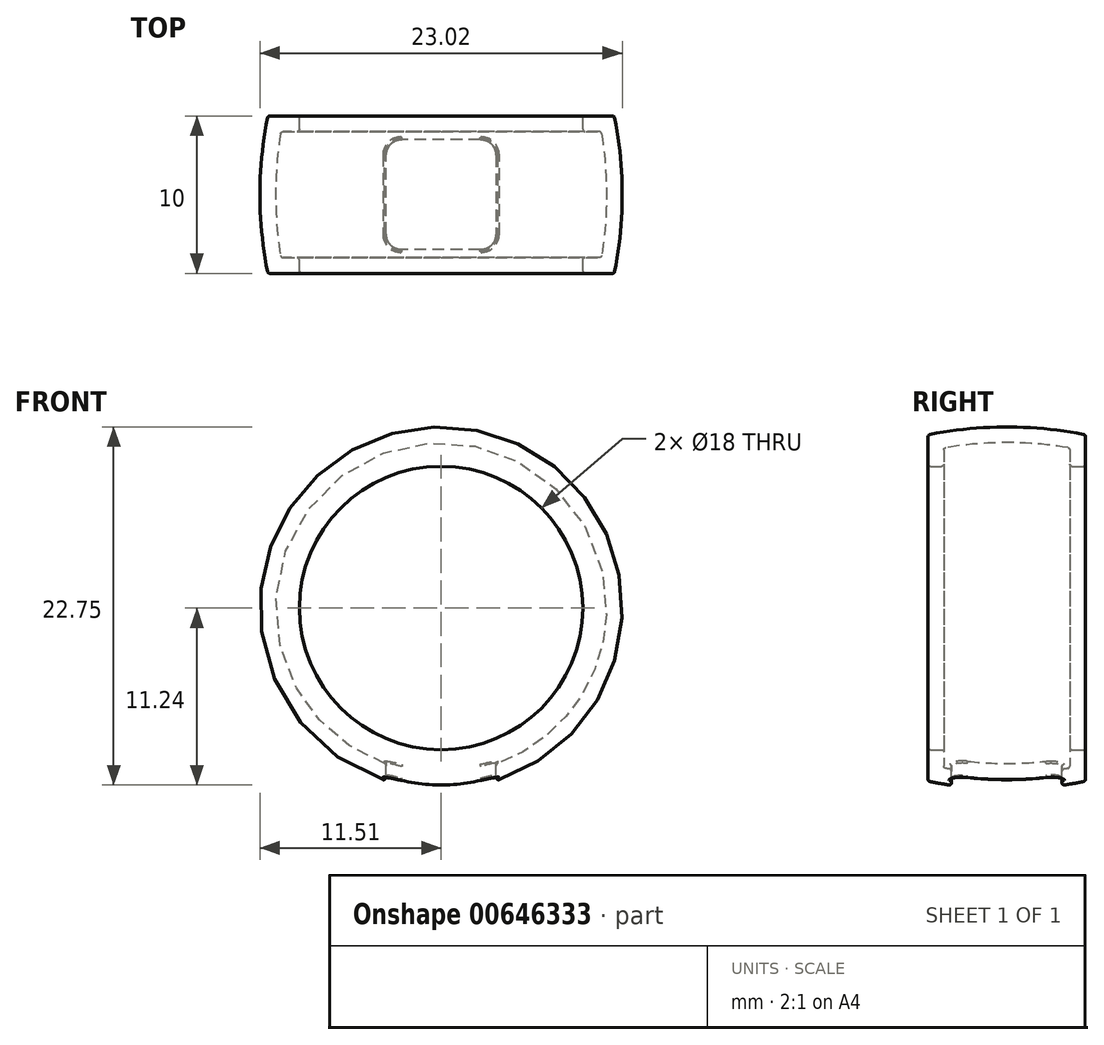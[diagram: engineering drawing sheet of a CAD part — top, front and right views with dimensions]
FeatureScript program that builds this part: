
annotation { "Feature Type Name" : "Feature", "Feature Type Description" : "" }
export const myFeature = defineFeature(function(context is Context, id is Id, definition is map)
    precondition{}
    {
        {
            var Q0;
            Q0=qCreatedBy(makeId("Top.planeOp"),FACE);
            var sketch = newSketch(context, id + "F0", { "sketchPlane" : qUnion([Q0])});
            skLineSegment(sketch, "E0", {"start": v(0, 0) * mm, "end": v(-9, 0) * mm, "construction": true});
            skLineSegment(sketch, "E1", {"start": v(-9, 5) * mm, "end": v(-9, -5) * mm});
            skLineSegment(sketch, "E2", {"start": v(-9, 5) * mm, "end": v(-11, 5) * mm});
            skLineSegment(sketch, "E3", {"start": v(-9, -5) * mm, "end": v(-11, -5) * mm});
            skArc(sketch, "E4", {"start": v(-11, 5) * mm, "mid": v(-11.5, 0) * mm, "end": v(-11, -5) * mm});
            skLineSegment(sketch, "E5", {"start": v(0, 0) * mm, "end": v(0, -20) * mm, "construction": true});
            skSolve(sketch);
        }
        {
            var Q0;
            Q0 = qSketchRegion(id + "F0", true);
            var Q1;
            Q1=sQuery(id+"F0.wireOp",EDGE,"E5");
            revolve(context, id + "F1", {"entities" : qUnion([Q0]), "axis" : qUnion([Q1]), "revolveType" : RevolveType.FULL});
        }
        {
            var Q0;
            Q0=makeQuery(id+"F1.opRevolve","SWEPT_FACE",FACE,{"disambiguationData":[OSD([sQuery(id+"F0.wireOp",EDGE,"E1")])]});
            shell(context, id + "F2", {"entities" : qUnion([Q0]), "thickness" : 1 * mm});
        }
        {
            var Q0;
            Q0=makeQuery(id+"F1.opRevolve","SWEPT_FACE",FACE,{"disambiguationData":[OSD([sQuery(id+"F0.wireOp",EDGE,"E4")])]});
            var Q1;
            Q1=makeQuery(id+"F1.opRevolve","SWEPT_EDGE",EDGE,{"disambiguationData":[OSD([sQuery(id+"F0.wireOp",EDGE,"E3"),sQuery(id+"F0.wireOp",EDGE,"E4")])]});
            var Q2;
            Q2=makeQuery(id+"F1.opRevolve","SWEPT_FACE",FACE,{"disambiguationData":[OSD([sQuery(id+"F0.wireOp",EDGE,"E3")])]});
            var Q3;
            Q3=makeQuery(id+"F1.opRevolve","SWEPT_EDGE",EDGE,{"disambiguationData":[OSD([sQuery(id+"F0.wireOp",EDGE,"E1"),sQuery(id+"F0.wireOp",EDGE,"E3")])]});
            var Q4;
            Q4=makeQuery(id+"F1.opRevolve","SWEPT_FACE",FACE,{"disambiguationData":[OSD([sQuery(id+"F0.wireOp",EDGE,"E2")])]});
            var Q5;
            Q5=makeQuery(id+"F1.opRevolve","SWEPT_EDGE",EDGE,{"disambiguationData":[OSD([sQuery(id+"F0.wireOp",EDGE,"E2"),sQuery(id+"F0.wireOp",EDGE,"E4")])]});
            var Q6;
            Q6=makeQuery(id+"F2.opShell","OFFSET_EDGE",EDGE,{"disambiguationData":[OSD([sQuery(id+"F0.wireOp",EDGE,"E1"),sQuery(id+"F0.wireOp",EDGE,"E2")])]});
            var Q7;
            Q7=makeQuery(id+"F1.opRevolve","SWEPT_EDGE",EDGE,{"disambiguationData":[OSD([sQuery(id+"F0.wireOp",EDGE,"E1"),sQuery(id+"F0.wireOp",EDGE,"E2")])]});
            var Q8;
            Q8=makeQuery(id+"F2.opShell","OFFSET_FACE",FACE,{"disambiguationData":[OSD([sQuery(id+"F0.wireOp",EDGE,"E1")])]});
            var Q9;
            Q9=makeQuery(id+"F2.opShell","OFFSET_EDGE",EDGE,{"disambiguationData":[OSD([sQuery(id+"F0.wireOp",EDGE,"E1"),sQuery(id+"F0.wireOp",EDGE,"E3")])]});
            var Q10;
            Q10=makeQuery(id+"F2.opShell","OFFSET_FACE",FACE,{"disambiguationData":[OSD([sQuery(id+"F0.wireOp",EDGE,"E2")])]});
            var Q11;
            Q11=makeQuery(id+"F2.opShell","OFFSET_EDGE",EDGE,{"disambiguationData":[OSD([sQuery(id+"F0.wireOp",EDGE,"E2"),sQuery(id+"F0.wireOp",EDGE,"E4")])]});
            var Q12;
            Q12=makeQuery(id+"F2.opShell","OFFSET_FACE",FACE,{"disambiguationData":[OSD([sQuery(id+"F0.wireOp",EDGE,"E3")])]});
            var Q13;
            Q13=makeQuery(id+"F2.opShell","OFFSET_FACE",FACE,{"disambiguationData":[OSD([sQuery(id+"F0.wireOp",EDGE,"E4")])]});
            var Q14;
            Q14=makeQuery(id+"F1.opRevolve","SWEPT_FACE",FACE,{"disambiguationData":[OSD([sQuery(id+"F0.wireOp",EDGE,"E1")])]});
            var Q15;
            Q15=makeQuery(id+"F2.opShell","OFFSET_EDGE",EDGE,{"disambiguationData":[OSD([sQuery(id+"F0.wireOp",EDGE,"E3"),sQuery(id+"F0.wireOp",EDGE,"E4")])]});
            fillet(context, id + "F3", {"entities" : qUnion([Q0, Q1, Q2, Q3, Q4, Q5, Q6, Q7, Q8, Q9, Q10, Q11, Q12, Q13, Q14, Q15]), "radius" : 0.15 * mm, "tangentPropagation" : true, "allowEdgeOverflow" : false});
        }
        {
            var Q0;
            Q0=qCreatedBy(makeId("Top.planeOp"),FACE);
            var sketch = newSketch(context, id + "F4", { "sketchPlane" : qUnion([Q0])});
            skLineSegment(sketch, "E6.bottom", {"start": v(2.5, 3.5) * mm, "end": v(-2.5, 3.5) * mm});
            skLineSegment(sketch, "E6.top", {"start": v(2.5, -3.5) * mm, "end": v(-2.5, -3.5) * mm});
            skLineSegment(sketch, "E6.left", {"start": v(3.5, 2.5) * mm, "end": v(3.5, -2.5) * mm});
            skLineSegment(sketch, "E6.right", {"start": v(-3.5, 2.5) * mm, "end": v(-3.5, -2.5) * mm});
            skPoint(sketch, "E6.middle", {"position": v(0, 0) * mm});
            skPoint(sketch, "E7.visualSharp", {"position": v(-3.5, 3.5) * mm});
            skArc(sketch, "E7.filletArc", {"start": v(-2.5, 3.5) * mm, "mid": v(-3.2, 3.2) * mm, "end": v(-3.5, 2.5) * mm});
            skPoint(sketch, "E8.visualSharp", {"position": v(3.5, 3.5) * mm});
            skArc(sketch, "E8.filletArc", {"start": v(3.5, 2.5) * mm, "mid": v(3.2, 3.2) * mm, "end": v(2.5, 3.5) * mm});
            skPoint(sketch, "E9.visualSharp", {"position": v(3.5, -3.5) * mm});
            skArc(sketch, "E9.filletArc", {"start": v(2.5, -3.5) * mm, "mid": v(3.2, -3.2) * mm, "end": v(3.5, -2.5) * mm});
            skPoint(sketch, "E10.visualSharp", {"position": v(-3.5, -3.5) * mm});
            skArc(sketch, "E10.filletArc", {"start": v(-3.5, -2.5) * mm, "mid": v(-3.2, -3.2) * mm, "end": v(-2.5, -3.5) * mm});
            skSolve(sketch);
        }
        {
            var Q0;
            Q0 = qSketchRegion(id + "F4", true);
            extrude(context, id + "F5", {"entities" : qUnion([Q0]), "operationType" : NewBodyOperationType.REMOVE, "endBound" : BoundingType.THROUGH_ALL, "oppositeDirection" : true, "depth" : 25 * mm, "offsetDistance" : 25 * mm});
        }
        {
            var Q0;
            Q0=makeQuery(id+"FbWcAx6KyJmYH2d_1.2.F5.boolean.opBoolean","INTERSECT",EDGE,{"derivedFrom":[makeQuery(id+"F1.opRevolve","SWEPT_FACE",FACE,{"disambiguationData":[OSD([sQuery(id+"F0.wireOp",EDGE,"E4")])]}),makeQuery(id+"FbWcAx6KyJmYH2d_1.2.F5.opExtrude","SWEPT_FACE",FACE,{"disambiguationData":[OSD([sQuery(id+"F4.wireOp",EDGE,"E6.right")])]})]});
            var Q1;
            {var subQ0=sQuery(id+"F0.wireOp",EDGE,"E3");Q1=makeQuery(id+"F3.opFillet","BLEND_EDGE",EDGE,{"blendedFrom":[makeQuery(id+"F1.opRevolve","SWEPT_EDGE",EDGE,{"disambiguationData":[OSD([sQuery(id+"F0.wireOp",EDGE,"E1"),subQ0])]}),makeQuery(id+"F1.opRevolve","SWEPT_FACE",FACE,{"disambiguationData":[OSD([subQ0])]})],"blendedInto":[makeQuery(id+"F1.opRevolve","SWEPT_FACE",FACE,{"disambiguationData":[OSD([subQ0])]})]});}
            var Q2;
            {var subQ0=sQuery(id+"F0.wireOp",EDGE,"E4");var subQ1=sQuery(id+"F0.wireOp",EDGE,"E3");Q2=makeQuery(id+"F3.opFillet","BLEND_FACE",FACE,{"disambiguationData":[OSD([subQ1,subQ0]),TDD([makeQuery(id+"F1.opRevolve","SWEPT_EDGE",EDGE,{"disambiguationData":[OSD([subQ1,subQ0])]})])]});}
            var Q3;
            {var subQ0=sQuery(id+"F0.wireOp",EDGE,"E1");Q3=makeQuery(id+"F3.opFillet","BLEND_EDGE",EDGE,{"blendedFrom":[makeQuery(id+"F1.opRevolve","SWEPT_EDGE",EDGE,{"disambiguationData":[OSD([subQ0,sQuery(id+"F0.wireOp",EDGE,"E3")])]}),makeQuery(id+"F1.opRevolve","SWEPT_FACE",FACE,{"disambiguationData":[OSD([subQ0])]})],"blendedInto":[makeQuery(id+"F1.opRevolve","SWEPT_FACE",FACE,{"disambiguationData":[OSD([subQ0])]})]});}
            var Q4;
            {var subQ0=sQuery(id+"F0.wireOp",EDGE,"E1");Q4=makeQuery(id+"F3.opFillet","BLEND_EDGE",EDGE,{"blendedFrom":[makeQuery(id+"F2.opShell","OFFSET_EDGE",EDGE,{"disambiguationData":[OSD([subQ0,sQuery(id+"F0.wireOp",EDGE,"E2")])]}),makeQuery(id+"F2.opShell","OFFSET_FACE",FACE,{"disambiguationData":[OSD([subQ0])]})],"blendedInto":[makeQuery(id+"F2.opShell","OFFSET_FACE",FACE,{"disambiguationData":[OSD([subQ0])]})]});}
            var Q5;
            {var subQ0=sQuery(id+"F0.wireOp",EDGE,"E4");var subQ1=sQuery(id+"F0.wireOp",EDGE,"E2");Q5=makeQuery(id+"F3.opFillet","BLEND_FACE",FACE,{"disambiguationData":[OSD([subQ1,subQ0]),TDD([makeQuery(id+"F1.opRevolve","SWEPT_EDGE",EDGE,{"disambiguationData":[OSD([subQ1,subQ0])]})])]});}
            var Q6;
            {var subQ0=sQuery(id+"F0.wireOp",EDGE,"E3");var subQ1=sQuery(id+"F0.wireOp",EDGE,"E1");Q6=makeQuery(id+"F3.opFillet","BLEND_FACE",FACE,{"disambiguationData":[OSD([subQ1,subQ0]),TDD([makeQuery(id+"F2.opShell","OFFSET_EDGE",EDGE,{"disambiguationData":[OSD([subQ1,subQ0])]})])]});}
            var Q7;
            {var subQ0=sQuery(id+"F0.wireOp",EDGE,"E4");var subQ1=sQuery(id+"F0.wireOp",EDGE,"E2");Q7=makeQuery(id+"F3.opFillet","BLEND_FACE",FACE,{"disambiguationData":[OSD([subQ1,subQ0]),TDD([makeQuery(id+"F2.opShell","OFFSET_EDGE",EDGE,{"disambiguationData":[OSD([subQ1,subQ0])]})])]});}
            var Q8;
            {var subQ0=sQuery(id+"F0.wireOp",EDGE,"E4");Q8=makeQuery(id+"F3.opFillet","BLEND_EDGE",EDGE,{"blendedFrom":[makeQuery(id+"F1.opRevolve","SWEPT_EDGE",EDGE,{"disambiguationData":[OSD([sQuery(id+"F0.wireOp",EDGE,"E2"),subQ0])]}),makeQuery(id+"F1.opRevolve","SWEPT_FACE",FACE,{"disambiguationData":[OSD([subQ0])]})],"blendedInto":[makeQuery(id+"F1.opRevolve","SWEPT_FACE",FACE,{"disambiguationData":[OSD([subQ0])]})]});}
            var Q9;
            Q9=makeQuery(id+"FbWcAx6KyJmYH2d_1.1.F5.boolean.opBoolean","INTERSECT",EDGE,{"derivedFrom":[makeQuery(id+"F1.opRevolve","SWEPT_FACE",FACE,{"disambiguationData":[OSD([sQuery(id+"F0.wireOp",EDGE,"E4")])]}),makeQuery(id+"FbWcAx6KyJmYH2d_1.1.F5.opExtrude","SWEPT_FACE",FACE,{"disambiguationData":[OSD([sQuery(id+"F4.wireOp",EDGE,"E6.bottom")])]})]});
            var Q10;
            Q10=makeQuery(id+"FbWcAx6KyJmYH2d_1.1.F5.boolean.opBoolean","COPY",FACE,{"derivedFrom":makeQuery(id+"FbWcAx6KyJmYH2d_1.1.F5.opExtrude","SWEPT_FACE",FACE,{"disambiguationData":[OSD([sQuery(id+"F4.wireOp",EDGE,"E9.filletArc")])]})});
            var Q11;
            Q11=makeQuery(id+"FbWcAx6KyJmYH2d_1.1.F5.boolean.opBoolean","INTERSECT",EDGE,{"derivedFrom":[makeQuery(id+"F1.opRevolve","SWEPT_FACE",FACE,{"disambiguationData":[OSD([sQuery(id+"F0.wireOp",EDGE,"E4")])]}),makeQuery(id+"FbWcAx6KyJmYH2d_1.1.F5.opExtrude","SWEPT_FACE",FACE,{"disambiguationData":[OSD([sQuery(id+"F4.wireOp",EDGE,"E6.top")])]})]});
            var Q12;
            Q12=makeQuery(id+"FbWcAx6KyJmYH2d_1.3.F5.boolean.opBoolean","INTERSECT",EDGE,{"derivedFrom":[makeQuery(id+"F1.opRevolve","SWEPT_FACE",FACE,{"disambiguationData":[OSD([sQuery(id+"F0.wireOp",EDGE,"E4")])]}),makeQuery(id+"FbWcAx6KyJmYH2d_1.3.F5.opExtrude","SWEPT_FACE",FACE,{"disambiguationData":[OSD([sQuery(id+"F4.wireOp",EDGE,"E6.top")])]})]});
            var Q13;
            Q13=makeQuery(id+"FbWcAx6KyJmYH2d_1.2.F5.boolean.opBoolean","COPY",FACE,{"derivedFrom":makeQuery(id+"FbWcAx6KyJmYH2d_1.2.F5.opExtrude","SWEPT_FACE",FACE,{"disambiguationData":[OSD([sQuery(id+"F4.wireOp",EDGE,"E6.right")])]})});
            var Q14;
            Q14=makeQuery(id+"FbWcAx6KyJmYH2d_1.3.F5.boolean.opBoolean","COPY",FACE,{"derivedFrom":makeQuery(id+"FbWcAx6KyJmYH2d_1.3.F5.opExtrude","SWEPT_FACE",FACE,{"disambiguationData":[OSD([sQuery(id+"F4.wireOp",EDGE,"E10.filletArc")])]})});
            var Q15;
            Q15=makeQuery(id+"FbWcAx6KyJmYH2d_1.2.F5.boolean.opBoolean","COPY",FACE,{"derivedFrom":makeQuery(id+"FbWcAx6KyJmYH2d_1.2.F5.opExtrude","SWEPT_FACE",FACE,{"disambiguationData":[OSD([sQuery(id+"F4.wireOp",EDGE,"E6.bottom")])]})});
            var Q16;
            Q16=makeQuery(id+"FbWcAx6KyJmYH2d_1.2.F5.boolean.opBoolean","COPY",FACE,{"derivedFrom":makeQuery(id+"FbWcAx6KyJmYH2d_1.2.F5.opExtrude","SWEPT_FACE",FACE,{"disambiguationData":[OSD([sQuery(id+"F4.wireOp",EDGE,"E8.filletArc")])]})});
            var Q17;
            Q17=makeQuery(id+"FbWcAx6KyJmYH2d_1.2.F5.boolean.opBoolean","COPY",FACE,{"derivedFrom":makeQuery(id+"FbWcAx6KyJmYH2d_1.2.F5.opExtrude","SWEPT_FACE",FACE,{"disambiguationData":[OSD([sQuery(id+"F4.wireOp",EDGE,"E9.filletArc")])]})});
            var Q18;
            Q18=makeQuery(id+"FbWcAx6KyJmYH2d_1.2.F5.boolean.opBoolean","INTERSECT",EDGE,{"derivedFrom":[makeQuery(id+"F1.opRevolve","SWEPT_FACE",FACE,{"disambiguationData":[OSD([sQuery(id+"F0.wireOp",EDGE,"E4")])]}),makeQuery(id+"FbWcAx6KyJmYH2d_1.2.F5.opExtrude","SWEPT_FACE",FACE,{"disambiguationData":[OSD([sQuery(id+"F4.wireOp",EDGE,"E6.bottom")])]})]});
            var Q19;
            Q19=makeQuery(id+"FbWcAx6KyJmYH2d_1.4.F5.boolean.opBoolean","INTERSECT",EDGE,{"derivedFrom":[makeQuery(id+"F1.opRevolve","SWEPT_FACE",FACE,{"disambiguationData":[OSD([sQuery(id+"F0.wireOp",EDGE,"E4")])]}),makeQuery(id+"FbWcAx6KyJmYH2d_1.4.F5.opExtrude","SWEPT_FACE",FACE,{"disambiguationData":[OSD([sQuery(id+"F4.wireOp",EDGE,"E6.right")])]})]});
            var Q20;
            {var subQ0=sQuery(id+"F0.wireOp",EDGE,"E2");Q20=makeQuery(id+"F3.opFillet","BLEND_EDGE",EDGE,{"blendedFrom":[makeQuery(id+"F2.opShell","OFFSET_EDGE",EDGE,{"disambiguationData":[OSD([sQuery(id+"F0.wireOp",EDGE,"E1"),subQ0])]}),makeQuery(id+"F2.opShell","OFFSET_FACE",FACE,{"disambiguationData":[OSD([subQ0])]})],"blendedInto":[makeQuery(id+"F2.opShell","OFFSET_FACE",FACE,{"disambiguationData":[OSD([subQ0])]})]});}
            var Q21;
            {var subQ0=sQuery(id+"F0.wireOp",EDGE,"E4");Q21=makeQuery(id+"F3.opFillet","BLEND_EDGE",EDGE,{"blendedFrom":[makeQuery(id+"F2.opShell","OFFSET_EDGE",EDGE,{"disambiguationData":[OSD([sQuery(id+"F0.wireOp",EDGE,"E2"),subQ0])]}),makeQuery(id+"F2.opShell","OFFSET_FACE",FACE,{"disambiguationData":[OSD([subQ0])]})],"blendedInto":[makeQuery(id+"F2.opShell","OFFSET_FACE",FACE,{"disambiguationData":[OSD([subQ0])]})]});}
            var Q22;
            Q22=makeQuery(id+"F1.opRevolve","SWEPT_FACE",FACE,{"disambiguationData":[OSD([sQuery(id+"F0.wireOp",EDGE,"E3")])]});
            var Q23;
            {var subQ0=sQuery(id+"F0.wireOp",EDGE,"E3");var subQ1=sQuery(id+"F0.wireOp",EDGE,"E1");Q23=makeQuery(id+"F3.opFillet","BLEND_FACE",FACE,{"disambiguationData":[OSD([subQ1,subQ0]),TDD([makeQuery(id+"F1.opRevolve","SWEPT_EDGE",EDGE,{"disambiguationData":[OSD([subQ1,subQ0])]})])]});}
            var Q24;
            {var subQ0=sQuery(id+"F0.wireOp",EDGE,"E3");Q24=makeQuery(id+"F3.opFillet","BLEND_EDGE",EDGE,{"blendedFrom":[makeQuery(id+"F1.opRevolve","SWEPT_EDGE",EDGE,{"disambiguationData":[OSD([subQ0,sQuery(id+"F0.wireOp",EDGE,"E4")])]}),makeQuery(id+"F1.opRevolve","SWEPT_FACE",FACE,{"disambiguationData":[OSD([subQ0])]})],"blendedInto":[makeQuery(id+"F1.opRevolve","SWEPT_FACE",FACE,{"disambiguationData":[OSD([subQ0])]})]});}
            var Q25;
            {var subQ0=sQuery(id+"F0.wireOp",EDGE,"E2");var subQ1=sQuery(id+"F0.wireOp",EDGE,"E1");Q25=makeQuery(id+"F3.opFillet","BLEND_FACE",FACE,{"disambiguationData":[OSD([subQ1,subQ0]),TDD([makeQuery(id+"F2.opShell","OFFSET_EDGE",EDGE,{"disambiguationData":[OSD([subQ1,subQ0])]})])]});}
            var Q26;
            {var subQ0=sQuery(id+"F0.wireOp",EDGE,"E2");var subQ1=sQuery(id+"F0.wireOp",EDGE,"E1");Q26=makeQuery(id+"F3.opFillet","BLEND_FACE",FACE,{"disambiguationData":[OSD([subQ1,subQ0]),TDD([makeQuery(id+"F1.opRevolve","SWEPT_EDGE",EDGE,{"disambiguationData":[OSD([subQ1,subQ0])]})])]});}
            var Q27;
            {var subQ0=sQuery(id+"F0.wireOp",EDGE,"E1");Q27=makeQuery(id+"F3.opFillet","BLEND_EDGE",EDGE,{"blendedFrom":[makeQuery(id+"F2.opShell","OFFSET_EDGE",EDGE,{"disambiguationData":[OSD([subQ0,sQuery(id+"F0.wireOp",EDGE,"E3")])]}),makeQuery(id+"F1.opRevolve","SWEPT_FACE",FACE,{"disambiguationData":[OSD([subQ0])]})],"blendedInto":[makeQuery(id+"F1.opRevolve","SWEPT_FACE",FACE,{"disambiguationData":[OSD([subQ0])]})]});}
            var Q28;
            {var subQ0=sQuery(id+"F0.wireOp",EDGE,"E1");Q28=makeQuery(id+"F3.opFillet","BLEND_EDGE",EDGE,{"blendedFrom":[makeQuery(id+"F1.opRevolve","SWEPT_EDGE",EDGE,{"disambiguationData":[OSD([subQ0,sQuery(id+"F0.wireOp",EDGE,"E2")])]}),makeQuery(id+"F2.opShell","OFFSET_FACE",FACE,{"disambiguationData":[OSD([subQ0])]})],"blendedInto":[makeQuery(id+"F2.opShell","OFFSET_FACE",FACE,{"disambiguationData":[OSD([subQ0])]})]});}
            var Q29;
            Q29=makeQuery(id+"FbWcAx6KyJmYH2d_1.6.F5.boolean.opBoolean","INTERSECT",EDGE,{"derivedFrom":[makeQuery(id+"F2.opShell","OFFSET_FACE",FACE,{"disambiguationData":[OSD([sQuery(id+"F0.wireOp",EDGE,"E4")])]}),makeQuery(id+"FbWcAx6KyJmYH2d_1.6.F5.opExtrude","SWEPT_FACE",FACE,{"disambiguationData":[OSD([sQuery(id+"F4.wireOp",EDGE,"E6.left")])]})]});
            var Q30;
            Q30=makeQuery(id+"FbWcAx6KyJmYH2d_1.1.F5.boolean.opBoolean","COPY",FACE,{"derivedFrom":makeQuery(id+"FbWcAx6KyJmYH2d_1.1.F5.opExtrude","SWEPT_FACE",FACE,{"disambiguationData":[OSD([sQuery(id+"F4.wireOp",EDGE,"E6.right")])]})});
            var Q31;
            {var subQ0=sQuery(id+"F0.wireOp",EDGE,"E4");Q31=makeQuery(id+"F3.opFillet","BLEND_EDGE",EDGE,{"blendedFrom":[makeQuery(id+"F1.opRevolve","SWEPT_EDGE",EDGE,{"disambiguationData":[OSD([sQuery(id+"F0.wireOp",EDGE,"E3"),subQ0])]}),makeQuery(id+"F1.opRevolve","SWEPT_FACE",FACE,{"disambiguationData":[OSD([subQ0])]})],"blendedInto":[makeQuery(id+"F1.opRevolve","SWEPT_FACE",FACE,{"disambiguationData":[OSD([subQ0])]})]});}
            var Q32;
            Q32=makeQuery(id+"F1.opRevolve","SWEPT_FACE",FACE,{"disambiguationData":[OSD([sQuery(id+"F0.wireOp",EDGE,"E1")])]});
            var Q33;
            Q33=makeQuery(id+"FbWcAx6KyJmYH2d_1.2.F5.boolean.opBoolean","INTERSECT",EDGE,{"derivedFrom":[makeQuery(id+"F2.opShell","OFFSET_FACE",FACE,{"disambiguationData":[OSD([sQuery(id+"F0.wireOp",EDGE,"E4")])]}),makeQuery(id+"FbWcAx6KyJmYH2d_1.2.F5.opExtrude","SWEPT_FACE",FACE,{"disambiguationData":[OSD([sQuery(id+"F4.wireOp",EDGE,"E6.right")])]})]});
            var Q34;
            Q34=makeQuery(id+"FbWcAx6KyJmYH2d_1.1.F5.boolean.opBoolean","INTERSECT",EDGE,{"derivedFrom":[makeQuery(id+"F1.opRevolve","SWEPT_FACE",FACE,{"disambiguationData":[OSD([sQuery(id+"F0.wireOp",EDGE,"E4")])]}),makeQuery(id+"FbWcAx6KyJmYH2d_1.1.F5.opExtrude","SWEPT_FACE",FACE,{"disambiguationData":[OSD([sQuery(id+"F4.wireOp",EDGE,"E6.left")])]})]});
            var Q35;
            Q35=makeQuery(id+"FbWcAx6KyJmYH2d_1.2.F5.boolean.opBoolean","INTERSECT",EDGE,{"derivedFrom":[makeQuery(id+"F1.opRevolve","SWEPT_FACE",FACE,{"disambiguationData":[OSD([sQuery(id+"F0.wireOp",EDGE,"E4")])]}),makeQuery(id+"FbWcAx6KyJmYH2d_1.2.F5.opExtrude","SWEPT_FACE",FACE,{"disambiguationData":[OSD([sQuery(id+"F4.wireOp",EDGE,"E6.top")])]})]});
            var Q36;
            Q36=makeQuery(id+"FbWcAx6KyJmYH2d_1.2.F5.boolean.opBoolean","INTERSECT",EDGE,{"derivedFrom":[makeQuery(id+"F1.opRevolve","SWEPT_FACE",FACE,{"disambiguationData":[OSD([sQuery(id+"F0.wireOp",EDGE,"E4")])]}),makeQuery(id+"FbWcAx6KyJmYH2d_1.2.F5.opExtrude","SWEPT_FACE",FACE,{"disambiguationData":[OSD([sQuery(id+"F4.wireOp",EDGE,"E6.left")])]})]});
            var Q37;
            Q37=makeQuery(id+"FbWcAx6KyJmYH2d_1.3.F5.boolean.opBoolean","INTERSECT",EDGE,{"derivedFrom":[makeQuery(id+"F2.opShell","OFFSET_FACE",FACE,{"disambiguationData":[OSD([sQuery(id+"F0.wireOp",EDGE,"E4")])]}),makeQuery(id+"FbWcAx6KyJmYH2d_1.3.F5.opExtrude","SWEPT_FACE",FACE,{"disambiguationData":[OSD([sQuery(id+"F4.wireOp",EDGE,"E6.left")])]})]});
            var Q38;
            Q38=makeQuery(id+"FbWcAx6KyJmYH2d_1.3.F5.boolean.opBoolean","INTERSECT",EDGE,{"derivedFrom":[makeQuery(id+"F1.opRevolve","SWEPT_FACE",FACE,{"disambiguationData":[OSD([sQuery(id+"F0.wireOp",EDGE,"E4")])]}),makeQuery(id+"FbWcAx6KyJmYH2d_1.3.F5.opExtrude","SWEPT_FACE",FACE,{"disambiguationData":[OSD([sQuery(id+"F4.wireOp",EDGE,"E6.right")])]})]});
            var Q39;
            Q39=makeQuery(id+"FbWcAx6KyJmYH2d_1.3.F5.boolean.opBoolean","COPY",FACE,{"derivedFrom":makeQuery(id+"FbWcAx6KyJmYH2d_1.3.F5.opExtrude","SWEPT_FACE",FACE,{"disambiguationData":[OSD([sQuery(id+"F4.wireOp",EDGE,"E6.bottom")])]})});
            var Q40;
            Q40=makeQuery(id+"FbWcAx6KyJmYH2d_1.3.F5.boolean.opBoolean","COPY",FACE,{"derivedFrom":makeQuery(id+"FbWcAx6KyJmYH2d_1.3.F5.opExtrude","SWEPT_FACE",FACE,{"disambiguationData":[OSD([sQuery(id+"F4.wireOp",EDGE,"E6.top")])]})});
            var Q41;
            Q41=makeQuery(id+"FbWcAx6KyJmYH2d_1.3.F5.boolean.opBoolean","COPY",FACE,{"derivedFrom":makeQuery(id+"FbWcAx6KyJmYH2d_1.3.F5.opExtrude","SWEPT_FACE",FACE,{"disambiguationData":[OSD([sQuery(id+"F4.wireOp",EDGE,"E6.left")])]})});
            var Q42;
            Q42=makeQuery(id+"FbWcAx6KyJmYH2d_1.2.F5.boolean.opBoolean","INTERSECT",EDGE,{"derivedFrom":[makeQuery(id+"F2.opShell","OFFSET_FACE",FACE,{"disambiguationData":[OSD([sQuery(id+"F0.wireOp",EDGE,"E4")])]}),makeQuery(id+"FbWcAx6KyJmYH2d_1.2.F5.opExtrude","SWEPT_FACE",FACE,{"disambiguationData":[OSD([sQuery(id+"F4.wireOp",EDGE,"E6.bottom")])]})]});
            var Q43;
            Q43=makeQuery(id+"FbWcAx6KyJmYH2d_1.4.F5.boolean.opBoolean","INTERSECT",EDGE,{"derivedFrom":[makeQuery(id+"F2.opShell","OFFSET_FACE",FACE,{"disambiguationData":[OSD([sQuery(id+"F0.wireOp",EDGE,"E4")])]}),makeQuery(id+"FbWcAx6KyJmYH2d_1.4.F5.opExtrude","SWEPT_FACE",FACE,{"disambiguationData":[OSD([sQuery(id+"F4.wireOp",EDGE,"E6.left")])]})]});
            var Q44;
            Q44=makeQuery(id+"FbWcAx6KyJmYH2d_1.1.F5.boolean.opBoolean","COPY",FACE,{"derivedFrom":makeQuery(id+"FbWcAx6KyJmYH2d_1.1.F5.opExtrude","SWEPT_FACE",FACE,{"disambiguationData":[OSD([sQuery(id+"F4.wireOp",EDGE,"E7.filletArc")])]})});
            var Q45;
            Q45=makeQuery(id+"FbWcAx6KyJmYH2d_1.1.F5.boolean.opBoolean","COPY",FACE,{"derivedFrom":makeQuery(id+"FbWcAx6KyJmYH2d_1.1.F5.opExtrude","SWEPT_FACE",FACE,{"disambiguationData":[OSD([sQuery(id+"F4.wireOp",EDGE,"E6.left")])]})});
            var Q46;
            Q46=makeQuery(id+"FbWcAx6KyJmYH2d_1.1.F5.boolean.opBoolean","COPY",FACE,{"derivedFrom":makeQuery(id+"FbWcAx6KyJmYH2d_1.1.F5.opExtrude","SWEPT_FACE",FACE,{"disambiguationData":[OSD([sQuery(id+"F4.wireOp",EDGE,"E6.bottom")])]})});
            var Q47;
            Q47=makeQuery(id+"FbWcAx6KyJmYH2d_1.1.F5.boolean.opBoolean","INTERSECT",EDGE,{"derivedFrom":[makeQuery(id+"F1.opRevolve","SWEPT_FACE",FACE,{"disambiguationData":[OSD([sQuery(id+"F0.wireOp",EDGE,"E4")])]}),makeQuery(id+"FbWcAx6KyJmYH2d_1.1.F5.opExtrude","SWEPT_FACE",FACE,{"disambiguationData":[OSD([sQuery(id+"F4.wireOp",EDGE,"E6.right")])]})]});
            var Q48;
            Q48=makeQuery(id+"F5.boolean.opBoolean","INTERSECT",EDGE,{"derivedFrom":[makeQuery(id+"F2.opShell","OFFSET_FACE",FACE,{"disambiguationData":[OSD([sQuery(id+"F0.wireOp",EDGE,"E4")])]}),makeQuery(id+"F5.opExtrude","SWEPT_FACE",FACE,{"disambiguationData":[OSD([sQuery(id+"F4.wireOp",EDGE,"E6.bottom")])]})]});
            var Q49;
            Q49=makeQuery(id+"F5.boolean.opBoolean","INTERSECT",EDGE,{"derivedFrom":[makeQuery(id+"F1.opRevolve","SWEPT_FACE",FACE,{"disambiguationData":[OSD([sQuery(id+"F0.wireOp",EDGE,"E4")])]}),makeQuery(id+"F5.opExtrude","SWEPT_FACE",FACE,{"disambiguationData":[OSD([sQuery(id+"F4.wireOp",EDGE,"E6.bottom")])]})]});
            var Q50;
            Q50=makeQuery(id+"F5.boolean.opBoolean","COPY",FACE,{"derivedFrom":makeQuery(id+"F5.opExtrude","SWEPT_FACE",FACE,{"disambiguationData":[OSD([sQuery(id+"F4.wireOp",EDGE,"E10.filletArc")])]})});
            var Q51;
            Q51=makeQuery(id+"F5.boolean.opBoolean","COPY",FACE,{"derivedFrom":makeQuery(id+"F5.opExtrude","SWEPT_FACE",FACE,{"disambiguationData":[OSD([sQuery(id+"F4.wireOp",EDGE,"E7.filletArc")])]})});
            var Q52;
            Q52=makeQuery(id+"F5.boolean.opBoolean","COPY",FACE,{"derivedFrom":makeQuery(id+"F5.opExtrude","SWEPT_FACE",FACE,{"disambiguationData":[OSD([sQuery(id+"F4.wireOp",EDGE,"E6.right")])]})});
            var Q53;
            Q53=makeQuery(id+"F5.boolean.opBoolean","COPY",FACE,{"derivedFrom":makeQuery(id+"F5.opExtrude","SWEPT_FACE",FACE,{"disambiguationData":[OSD([sQuery(id+"F4.wireOp",EDGE,"E6.bottom")])]})});
            var Q54;
            Q54=makeQuery(id+"F5.boolean.opBoolean","INTERSECT",EDGE,{"derivedFrom":[makeQuery(id+"F2.opShell","OFFSET_FACE",FACE,{"disambiguationData":[OSD([sQuery(id+"F0.wireOp",EDGE,"E4")])]}),makeQuery(id+"F5.opExtrude","SWEPT_FACE",FACE,{"disambiguationData":[OSD([sQuery(id+"F4.wireOp",EDGE,"E6.right")])]})]});
            var Q55;
            Q55=makeQuery(id+"F5.boolean.opBoolean","INTERSECT",EDGE,{"derivedFrom":[makeQuery(id+"F1.opRevolve","SWEPT_FACE",FACE,{"disambiguationData":[OSD([sQuery(id+"F0.wireOp",EDGE,"E4")])]}),makeQuery(id+"F5.opExtrude","SWEPT_FACE",FACE,{"disambiguationData":[OSD([sQuery(id+"F4.wireOp",EDGE,"E6.right")])]})]});
            var Q56;
            Q56=makeQuery(id+"F2.opShell","OFFSET_FACE",FACE,{"disambiguationData":[OSD([sQuery(id+"F0.wireOp",EDGE,"E1")])]});
            var Q57;
            {var subQ0=sQuery(id+"F0.wireOp",EDGE,"E2");Q57=makeQuery(id+"F3.opFillet","BLEND_EDGE",EDGE,{"blendedFrom":[makeQuery(id+"F2.opShell","OFFSET_EDGE",EDGE,{"disambiguationData":[OSD([subQ0,sQuery(id+"F0.wireOp",EDGE,"E4")])]}),makeQuery(id+"F2.opShell","OFFSET_FACE",FACE,{"disambiguationData":[OSD([subQ0])]})],"blendedInto":[makeQuery(id+"F2.opShell","OFFSET_FACE",FACE,{"disambiguationData":[OSD([subQ0])]})]});}
            var Q58;
            Q58=makeQuery(id+"FbWcAx6KyJmYH2d_1.6.F5.boolean.opBoolean","INTERSECT",EDGE,{"derivedFrom":[makeQuery(id+"F2.opShell","OFFSET_FACE",FACE,{"disambiguationData":[OSD([sQuery(id+"F0.wireOp",EDGE,"E4")])]}),makeQuery(id+"FbWcAx6KyJmYH2d_1.6.F5.opExtrude","SWEPT_FACE",FACE,{"disambiguationData":[OSD([sQuery(id+"F4.wireOp",EDGE,"E9.filletArc")])]})]});
            var Q59;
            Q59=makeQuery(id+"FbWcAx6KyJmYH2d_1.6.F5.boolean.opBoolean","INTERSECT",EDGE,{"derivedFrom":[makeQuery(id+"F1.opRevolve","SWEPT_FACE",FACE,{"disambiguationData":[OSD([sQuery(id+"F0.wireOp",EDGE,"E4")])]}),makeQuery(id+"FbWcAx6KyJmYH2d_1.6.F5.opExtrude","SWEPT_FACE",FACE,{"disambiguationData":[OSD([sQuery(id+"F4.wireOp",EDGE,"E8.filletArc")])]})]});
            var Q60;
            Q60=makeQuery(id+"FbWcAx6KyJmYH2d_1.6.F5.boolean.opBoolean","INTERSECT",EDGE,{"derivedFrom":[makeQuery(id+"F2.opShell","OFFSET_FACE",FACE,{"disambiguationData":[OSD([sQuery(id+"F0.wireOp",EDGE,"E4")])]}),makeQuery(id+"FbWcAx6KyJmYH2d_1.6.F5.opExtrude","SWEPT_FACE",FACE,{"disambiguationData":[OSD([sQuery(id+"F4.wireOp",EDGE,"E8.filletArc")])]})]});
            var Q61;
            Q61=makeQuery(id+"FbWcAx6KyJmYH2d_1.6.F5.boolean.opBoolean","INTERSECT",EDGE,{"derivedFrom":[makeQuery(id+"F2.opShell","OFFSET_FACE",FACE,{"disambiguationData":[OSD([sQuery(id+"F0.wireOp",EDGE,"E4")])]}),makeQuery(id+"FbWcAx6KyJmYH2d_1.6.F5.opExtrude","SWEPT_FACE",FACE,{"disambiguationData":[OSD([sQuery(id+"F4.wireOp",EDGE,"E7.filletArc")])]})]});
            var Q62;
            Q62=makeQuery(id+"FbWcAx6KyJmYH2d_1.6.F5.boolean.opBoolean","INTERSECT",EDGE,{"derivedFrom":[makeQuery(id+"F1.opRevolve","SWEPT_FACE",FACE,{"disambiguationData":[OSD([sQuery(id+"F0.wireOp",EDGE,"E4")])]}),makeQuery(id+"FbWcAx6KyJmYH2d_1.6.F5.opExtrude","SWEPT_FACE",FACE,{"disambiguationData":[OSD([sQuery(id+"F4.wireOp",EDGE,"E7.filletArc")])]})]});
            var Q63;
            Q63=makeQuery(id+"FbWcAx6KyJmYH2d_1.5.F5.boolean.opBoolean","INTERSECT",EDGE,{"derivedFrom":[makeQuery(id+"F2.opShell","OFFSET_FACE",FACE,{"disambiguationData":[OSD([sQuery(id+"F0.wireOp",EDGE,"E4")])]}),makeQuery(id+"FbWcAx6KyJmYH2d_1.5.F5.opExtrude","SWEPT_FACE",FACE,{"disambiguationData":[OSD([sQuery(id+"F4.wireOp",EDGE,"E9.filletArc")])]})]});
            var Q64;
            Q64=makeQuery(id+"FbWcAx6KyJmYH2d_1.5.F5.boolean.opBoolean","INTERSECT",EDGE,{"derivedFrom":[makeQuery(id+"F1.opRevolve","SWEPT_FACE",FACE,{"disambiguationData":[OSD([sQuery(id+"F0.wireOp",EDGE,"E4")])]}),makeQuery(id+"FbWcAx6KyJmYH2d_1.5.F5.opExtrude","SWEPT_FACE",FACE,{"disambiguationData":[OSD([sQuery(id+"F4.wireOp",EDGE,"E8.filletArc")])]})]});
            var Q65;
            Q65=makeQuery(id+"FbWcAx6KyJmYH2d_1.5.F5.boolean.opBoolean","INTERSECT",EDGE,{"derivedFrom":[makeQuery(id+"F2.opShell","OFFSET_FACE",FACE,{"disambiguationData":[OSD([sQuery(id+"F0.wireOp",EDGE,"E4")])]}),makeQuery(id+"FbWcAx6KyJmYH2d_1.5.F5.opExtrude","SWEPT_FACE",FACE,{"disambiguationData":[OSD([sQuery(id+"F4.wireOp",EDGE,"E8.filletArc")])]})]});
            var Q66;
            Q66=makeQuery(id+"FbWcAx6KyJmYH2d_1.5.F5.boolean.opBoolean","INTERSECT",EDGE,{"derivedFrom":[makeQuery(id+"F2.opShell","OFFSET_FACE",FACE,{"disambiguationData":[OSD([sQuery(id+"F0.wireOp",EDGE,"E4")])]}),makeQuery(id+"FbWcAx6KyJmYH2d_1.5.F5.opExtrude","SWEPT_FACE",FACE,{"disambiguationData":[OSD([sQuery(id+"F4.wireOp",EDGE,"E7.filletArc")])]})]});
            var Q67;
            Q67=makeQuery(id+"FbWcAx6KyJmYH2d_1.4.F5.boolean.opBoolean","INTERSECT",EDGE,{"derivedFrom":[makeQuery(id+"F1.opRevolve","SWEPT_FACE",FACE,{"disambiguationData":[OSD([sQuery(id+"F0.wireOp",EDGE,"E4")])]}),makeQuery(id+"FbWcAx6KyJmYH2d_1.4.F5.opExtrude","SWEPT_FACE",FACE,{"disambiguationData":[OSD([sQuery(id+"F4.wireOp",EDGE,"E10.filletArc")])]})]});
            var Q68;
            Q68=makeQuery(id+"FbWcAx6KyJmYH2d_1.4.F5.boolean.opBoolean","INTERSECT",EDGE,{"derivedFrom":[makeQuery(id+"F1.opRevolve","SWEPT_FACE",FACE,{"disambiguationData":[OSD([sQuery(id+"F0.wireOp",EDGE,"E4")])]}),makeQuery(id+"FbWcAx6KyJmYH2d_1.4.F5.opExtrude","SWEPT_FACE",FACE,{"disambiguationData":[OSD([sQuery(id+"F4.wireOp",EDGE,"E8.filletArc")])]})]});
            var Q69;
            Q69=makeQuery(id+"FbWcAx6KyJmYH2d_1.4.F5.boolean.opBoolean","INTERSECT",EDGE,{"derivedFrom":[makeQuery(id+"F1.opRevolve","SWEPT_FACE",FACE,{"disambiguationData":[OSD([sQuery(id+"F0.wireOp",EDGE,"E4")])]}),makeQuery(id+"FbWcAx6KyJmYH2d_1.4.F5.opExtrude","SWEPT_FACE",FACE,{"disambiguationData":[OSD([sQuery(id+"F4.wireOp",EDGE,"E7.filletArc")])]})]});
            var Q70;
            Q70=makeQuery(id+"FbWcAx6KyJmYH2d_1.3.F5.boolean.opBoolean","INTERSECT",EDGE,{"derivedFrom":[makeQuery(id+"F1.opRevolve","SWEPT_FACE",FACE,{"disambiguationData":[OSD([sQuery(id+"F0.wireOp",EDGE,"E4")])]}),makeQuery(id+"FbWcAx6KyJmYH2d_1.3.F5.opExtrude","SWEPT_FACE",FACE,{"disambiguationData":[OSD([sQuery(id+"F4.wireOp",EDGE,"E10.filletArc")])]})]});
            var Q71;
            Q71=makeQuery(id+"FbWcAx6KyJmYH2d_1.3.F5.boolean.opBoolean","INTERSECT",EDGE,{"derivedFrom":[makeQuery(id+"F1.opRevolve","SWEPT_FACE",FACE,{"disambiguationData":[OSD([sQuery(id+"F0.wireOp",EDGE,"E4")])]}),makeQuery(id+"FbWcAx6KyJmYH2d_1.3.F5.opExtrude","SWEPT_FACE",FACE,{"disambiguationData":[OSD([sQuery(id+"F4.wireOp",EDGE,"E9.filletArc")])]})]});
            var Q72;
            Q72=makeQuery(id+"FbWcAx6KyJmYH2d_1.3.F5.boolean.opBoolean","INTERSECT",EDGE,{"derivedFrom":[makeQuery(id+"F2.opShell","OFFSET_FACE",FACE,{"disambiguationData":[OSD([sQuery(id+"F0.wireOp",EDGE,"E4")])]}),makeQuery(id+"FbWcAx6KyJmYH2d_1.3.F5.opExtrude","SWEPT_FACE",FACE,{"disambiguationData":[OSD([sQuery(id+"F4.wireOp",EDGE,"E8.filletArc")])]})]});
            var Q73;
            Q73=makeQuery(id+"FbWcAx6KyJmYH2d_1.3.F5.boolean.opBoolean","INTERSECT",EDGE,{"derivedFrom":[makeQuery(id+"F1.opRevolve","SWEPT_FACE",FACE,{"disambiguationData":[OSD([sQuery(id+"F0.wireOp",EDGE,"E4")])]}),makeQuery(id+"FbWcAx6KyJmYH2d_1.3.F5.opExtrude","SWEPT_FACE",FACE,{"disambiguationData":[OSD([sQuery(id+"F4.wireOp",EDGE,"E7.filletArc")])]})]});
            var Q74;
            Q74=makeQuery(id+"FbWcAx6KyJmYH2d_1.2.F5.boolean.opBoolean","INTERSECT",EDGE,{"derivedFrom":[makeQuery(id+"F1.opRevolve","SWEPT_FACE",FACE,{"disambiguationData":[OSD([sQuery(id+"F0.wireOp",EDGE,"E4")])]}),makeQuery(id+"FbWcAx6KyJmYH2d_1.2.F5.opExtrude","SWEPT_FACE",FACE,{"disambiguationData":[OSD([sQuery(id+"F4.wireOp",EDGE,"E9.filletArc")])]})]});
            var Q75;
            Q75=makeQuery(id+"FbWcAx6KyJmYH2d_1.2.F5.boolean.opBoolean","INTERSECT",EDGE,{"derivedFrom":[makeQuery(id+"F2.opShell","OFFSET_FACE",FACE,{"disambiguationData":[OSD([sQuery(id+"F0.wireOp",EDGE,"E4")])]}),makeQuery(id+"FbWcAx6KyJmYH2d_1.2.F5.opExtrude","SWEPT_FACE",FACE,{"disambiguationData":[OSD([sQuery(id+"F4.wireOp",EDGE,"E7.filletArc")])]})]});
            var Q76;
            Q76=makeQuery(id+"FbWcAx6KyJmYH2d_1.2.F5.boolean.opBoolean","INTERSECT",EDGE,{"derivedFrom":[makeQuery(id+"F1.opRevolve","SWEPT_FACE",FACE,{"disambiguationData":[OSD([sQuery(id+"F0.wireOp",EDGE,"E4")])]}),makeQuery(id+"FbWcAx6KyJmYH2d_1.2.F5.opExtrude","SWEPT_FACE",FACE,{"disambiguationData":[OSD([sQuery(id+"F4.wireOp",EDGE,"E10.filletArc")])]})]});
            var Q77;
            Q77=makeQuery(id+"FbWcAx6KyJmYH2d_1.2.F5.boolean.opBoolean","INTERSECT",EDGE,{"derivedFrom":[makeQuery(id+"F1.opRevolve","SWEPT_FACE",FACE,{"disambiguationData":[OSD([sQuery(id+"F0.wireOp",EDGE,"E4")])]}),makeQuery(id+"FbWcAx6KyJmYH2d_1.2.F5.opExtrude","SWEPT_FACE",FACE,{"disambiguationData":[OSD([sQuery(id+"F4.wireOp",EDGE,"E8.filletArc")])]})]});
            var Q78;
            Q78=makeQuery(id+"FbWcAx6KyJmYH2d_1.2.F5.boolean.opBoolean","INTERSECT",EDGE,{"derivedFrom":[makeQuery(id+"F1.opRevolve","SWEPT_FACE",FACE,{"disambiguationData":[OSD([sQuery(id+"F0.wireOp",EDGE,"E4")])]}),makeQuery(id+"FbWcAx6KyJmYH2d_1.2.F5.opExtrude","SWEPT_FACE",FACE,{"disambiguationData":[OSD([sQuery(id+"F4.wireOp",EDGE,"E7.filletArc")])]})]});
            var Q79;
            Q79=makeQuery(id+"FbWcAx6KyJmYH2d_1.1.F5.boolean.opBoolean","INTERSECT",EDGE,{"derivedFrom":[makeQuery(id+"F1.opRevolve","SWEPT_FACE",FACE,{"disambiguationData":[OSD([sQuery(id+"F0.wireOp",EDGE,"E4")])]}),makeQuery(id+"FbWcAx6KyJmYH2d_1.1.F5.opExtrude","SWEPT_FACE",FACE,{"disambiguationData":[OSD([sQuery(id+"F4.wireOp",EDGE,"E9.filletArc")])]})]});
            var Q80;
            Q80=makeQuery(id+"FbWcAx6KyJmYH2d_1.1.F5.boolean.opBoolean","INTERSECT",EDGE,{"derivedFrom":[makeQuery(id+"F1.opRevolve","SWEPT_FACE",FACE,{"disambiguationData":[OSD([sQuery(id+"F0.wireOp",EDGE,"E4")])]}),makeQuery(id+"FbWcAx6KyJmYH2d_1.1.F5.opExtrude","SWEPT_FACE",FACE,{"disambiguationData":[OSD([sQuery(id+"F4.wireOp",EDGE,"E8.filletArc")])]})]});
            var Q81;
            Q81=makeQuery(id+"FbWcAx6KyJmYH2d_1.1.F5.boolean.opBoolean","INTERSECT",EDGE,{"derivedFrom":[makeQuery(id+"F1.opRevolve","SWEPT_FACE",FACE,{"disambiguationData":[OSD([sQuery(id+"F0.wireOp",EDGE,"E4")])]}),makeQuery(id+"FbWcAx6KyJmYH2d_1.1.F5.opExtrude","SWEPT_FACE",FACE,{"disambiguationData":[OSD([sQuery(id+"F4.wireOp",EDGE,"E7.filletArc")])]})]});
            var Q82;
            Q82=makeQuery(id+"F5.boolean.opBoolean","INTERSECT",EDGE,{"derivedFrom":[makeQuery(id+"F2.opShell","OFFSET_FACE",FACE,{"disambiguationData":[OSD([sQuery(id+"F0.wireOp",EDGE,"E4")])]}),makeQuery(id+"F5.opExtrude","SWEPT_FACE",FACE,{"disambiguationData":[OSD([sQuery(id+"F4.wireOp",EDGE,"E7.filletArc")])]})]});
            var Q83;
            Q83=makeQuery(id+"FbWcAx6KyJmYH2d_1.6.F5.boolean.opBoolean","INTERSECT",EDGE,{"derivedFrom":[makeQuery(id+"F1.opRevolve","SWEPT_FACE",FACE,{"disambiguationData":[OSD([sQuery(id+"F0.wireOp",EDGE,"E4")])]}),makeQuery(id+"FbWcAx6KyJmYH2d_1.6.F5.opExtrude","SWEPT_FACE",FACE,{"disambiguationData":[OSD([sQuery(id+"F4.wireOp",EDGE,"E6.left")])]})]});
            var Q84;
            Q84=makeQuery(id+"F5.boolean.opBoolean","INTERSECT",EDGE,{"derivedFrom":[makeQuery(id+"F1.opRevolve","SWEPT_FACE",FACE,{"disambiguationData":[OSD([sQuery(id+"F0.wireOp",EDGE,"E4")])]}),makeQuery(id+"F5.opExtrude","SWEPT_FACE",FACE,{"disambiguationData":[OSD([sQuery(id+"F4.wireOp",EDGE,"E7.filletArc")])]})]});
            var Q85;
            Q85=makeQuery(id+"F2.opShell","OFFSET_FACE",FACE,{"disambiguationData":[OSD([sQuery(id+"F0.wireOp",EDGE,"E4")])]});
            var Q86;
            Q86=makeQuery(id+"FbWcAx6KyJmYH2d_1.6.F5.boolean.opBoolean","INTERSECT",EDGE,{"derivedFrom":[makeQuery(id+"F2.opShell","OFFSET_FACE",FACE,{"disambiguationData":[OSD([sQuery(id+"F0.wireOp",EDGE,"E4")])]}),makeQuery(id+"FbWcAx6KyJmYH2d_1.6.F5.opExtrude","SWEPT_FACE",FACE,{"disambiguationData":[OSD([sQuery(id+"F4.wireOp",EDGE,"E6.bottom")])]})]});
            var Q87;
            Q87=makeQuery(id+"F1.opRevolve","SWEPT_FACE",FACE,{"disambiguationData":[OSD([sQuery(id+"F0.wireOp",EDGE,"E4")])]});
            var Q88;
            Q88=makeQuery(id+"FbWcAx6KyJmYH2d_1.6.F5.boolean.opBoolean","INTERSECT",EDGE,{"derivedFrom":[makeQuery(id+"F1.opRevolve","SWEPT_FACE",FACE,{"disambiguationData":[OSD([sQuery(id+"F0.wireOp",EDGE,"E4")])]}),makeQuery(id+"FbWcAx6KyJmYH2d_1.6.F5.opExtrude","SWEPT_FACE",FACE,{"disambiguationData":[OSD([sQuery(id+"F4.wireOp",EDGE,"E6.bottom")])]})]});
            var Q89;
            Q89=makeQuery(id+"FbWcAx6KyJmYH2d_1.6.F5.boolean.opBoolean","COPY",FACE,{"derivedFrom":makeQuery(id+"FbWcAx6KyJmYH2d_1.6.F5.opExtrude","SWEPT_FACE",FACE,{"disambiguationData":[OSD([sQuery(id+"F4.wireOp",EDGE,"E10.filletArc")])]})});
            var Q90;
            Q90=makeQuery(id+"FbWcAx6KyJmYH2d_1.6.F5.boolean.opBoolean","COPY",FACE,{"derivedFrom":makeQuery(id+"FbWcAx6KyJmYH2d_1.6.F5.opExtrude","SWEPT_FACE",FACE,{"disambiguationData":[OSD([sQuery(id+"F4.wireOp",EDGE,"E9.filletArc")])]})});
            var Q91;
            Q91=makeQuery(id+"FbWcAx6KyJmYH2d_1.6.F5.boolean.opBoolean","COPY",FACE,{"derivedFrom":makeQuery(id+"FbWcAx6KyJmYH2d_1.6.F5.opExtrude","SWEPT_FACE",FACE,{"disambiguationData":[OSD([sQuery(id+"F4.wireOp",EDGE,"E8.filletArc")])]})});
            var Q92;
            Q92=makeQuery(id+"FbWcAx6KyJmYH2d_1.6.F5.boolean.opBoolean","COPY",FACE,{"derivedFrom":makeQuery(id+"FbWcAx6KyJmYH2d_1.6.F5.opExtrude","SWEPT_FACE",FACE,{"disambiguationData":[OSD([sQuery(id+"F4.wireOp",EDGE,"E7.filletArc")])]})});
            var Q93;
            Q93=makeQuery(id+"FbWcAx6KyJmYH2d_1.6.F5.boolean.opBoolean","COPY",FACE,{"derivedFrom":makeQuery(id+"FbWcAx6KyJmYH2d_1.6.F5.opExtrude","SWEPT_FACE",FACE,{"disambiguationData":[OSD([sQuery(id+"F4.wireOp",EDGE,"E6.left")])]})});
            var Q94;
            Q94=makeQuery(id+"FbWcAx6KyJmYH2d_1.6.F5.boolean.opBoolean","COPY",FACE,{"derivedFrom":makeQuery(id+"FbWcAx6KyJmYH2d_1.6.F5.opExtrude","SWEPT_FACE",FACE,{"disambiguationData":[OSD([sQuery(id+"F4.wireOp",EDGE,"E6.right")])]})});
            var Q95;
            Q95=makeQuery(id+"FbWcAx6KyJmYH2d_1.6.F5.boolean.opBoolean","COPY",FACE,{"derivedFrom":makeQuery(id+"FbWcAx6KyJmYH2d_1.6.F5.opExtrude","SWEPT_FACE",FACE,{"disambiguationData":[OSD([sQuery(id+"F4.wireOp",EDGE,"E6.bottom")])]})});
            var Q96;
            Q96=makeQuery(id+"FbWcAx6KyJmYH2d_1.6.F5.boolean.opBoolean","INTERSECT",EDGE,{"derivedFrom":[makeQuery(id+"F2.opShell","OFFSET_FACE",FACE,{"disambiguationData":[OSD([sQuery(id+"F0.wireOp",EDGE,"E4")])]}),makeQuery(id+"FbWcAx6KyJmYH2d_1.6.F5.opExtrude","SWEPT_FACE",FACE,{"disambiguationData":[OSD([sQuery(id+"F4.wireOp",EDGE,"E6.right")])]})]});
            var Q97;
            Q97=makeQuery(id+"FbWcAx6KyJmYH2d_1.5.F5.boolean.opBoolean","INTERSECT",EDGE,{"derivedFrom":[makeQuery(id+"F1.opRevolve","SWEPT_FACE",FACE,{"disambiguationData":[OSD([sQuery(id+"F0.wireOp",EDGE,"E4")])]}),makeQuery(id+"FbWcAx6KyJmYH2d_1.5.F5.opExtrude","SWEPT_FACE",FACE,{"disambiguationData":[OSD([sQuery(id+"F4.wireOp",EDGE,"E6.left")])]})]});
            var Q98;
            Q98=makeQuery(id+"FbWcAx6KyJmYH2d_1.5.F5.boolean.opBoolean","COPY",FACE,{"derivedFrom":makeQuery(id+"FbWcAx6KyJmYH2d_1.5.F5.opExtrude","SWEPT_FACE",FACE,{"disambiguationData":[OSD([sQuery(id+"F4.wireOp",EDGE,"E8.filletArc")])]})});
            var Q99;
            Q99=makeQuery(id+"FbWcAx6KyJmYH2d_1.5.F5.boolean.opBoolean","COPY",FACE,{"derivedFrom":makeQuery(id+"FbWcAx6KyJmYH2d_1.5.F5.opExtrude","SWEPT_FACE",FACE,{"disambiguationData":[OSD([sQuery(id+"F4.wireOp",EDGE,"E6.left")])]})});
            var Q100;
            Q100=makeQuery(id+"FbWcAx6KyJmYH2d_1.5.F5.boolean.opBoolean","COPY",FACE,{"derivedFrom":makeQuery(id+"FbWcAx6KyJmYH2d_1.5.F5.opExtrude","SWEPT_FACE",FACE,{"disambiguationData":[OSD([sQuery(id+"F4.wireOp",EDGE,"E6.bottom")])]})});
            var Q101;
            Q101=makeQuery(id+"FbWcAx6KyJmYH2d_1.4.F5.boolean.opBoolean","INTERSECT",EDGE,{"derivedFrom":[makeQuery(id+"F1.opRevolve","SWEPT_FACE",FACE,{"disambiguationData":[OSD([sQuery(id+"F0.wireOp",EDGE,"E4")])]}),makeQuery(id+"FbWcAx6KyJmYH2d_1.4.F5.opExtrude","SWEPT_FACE",FACE,{"disambiguationData":[OSD([sQuery(id+"F4.wireOp",EDGE,"E6.left")])]})]});
            var Q102;
            Q102=makeQuery(id+"FbWcAx6KyJmYH2d_1.4.F5.boolean.opBoolean","INTERSECT",EDGE,{"derivedFrom":[makeQuery(id+"F2.opShell","OFFSET_FACE",FACE,{"disambiguationData":[OSD([sQuery(id+"F0.wireOp",EDGE,"E4")])]}),makeQuery(id+"FbWcAx6KyJmYH2d_1.4.F5.opExtrude","SWEPT_FACE",FACE,{"disambiguationData":[OSD([sQuery(id+"F4.wireOp",EDGE,"E6.bottom")])]})]});
            var Q103;
            Q103=makeQuery(id+"FbWcAx6KyJmYH2d_1.4.F5.boolean.opBoolean","INTERSECT",EDGE,{"derivedFrom":[makeQuery(id+"F1.opRevolve","SWEPT_FACE",FACE,{"disambiguationData":[OSD([sQuery(id+"F0.wireOp",EDGE,"E4")])]}),makeQuery(id+"FbWcAx6KyJmYH2d_1.4.F5.opExtrude","SWEPT_FACE",FACE,{"disambiguationData":[OSD([sQuery(id+"F4.wireOp",EDGE,"E6.top")])]})]});
            var Q104;
            Q104=makeQuery(id+"FbWcAx6KyJmYH2d_1.4.F5.boolean.opBoolean","INTERSECT",EDGE,{"derivedFrom":[makeQuery(id+"F1.opRevolve","SWEPT_FACE",FACE,{"disambiguationData":[OSD([sQuery(id+"F0.wireOp",EDGE,"E4")])]}),makeQuery(id+"FbWcAx6KyJmYH2d_1.4.F5.opExtrude","SWEPT_FACE",FACE,{"disambiguationData":[OSD([sQuery(id+"F4.wireOp",EDGE,"E6.bottom")])]})]});
            var Q105;
            Q105=makeQuery(id+"FbWcAx6KyJmYH2d_1.4.F5.boolean.opBoolean","COPY",FACE,{"derivedFrom":makeQuery(id+"FbWcAx6KyJmYH2d_1.4.F5.opExtrude","SWEPT_FACE",FACE,{"disambiguationData":[OSD([sQuery(id+"F4.wireOp",EDGE,"E10.filletArc")])]})});
            var Q106;
            Q106=makeQuery(id+"FbWcAx6KyJmYH2d_1.4.F5.boolean.opBoolean","COPY",FACE,{"derivedFrom":makeQuery(id+"FbWcAx6KyJmYH2d_1.4.F5.opExtrude","SWEPT_FACE",FACE,{"disambiguationData":[OSD([sQuery(id+"F4.wireOp",EDGE,"E8.filletArc")])]})});
            var Q107;
            Q107=makeQuery(id+"FbWcAx6KyJmYH2d_1.4.F5.boolean.opBoolean","COPY",FACE,{"derivedFrom":makeQuery(id+"FbWcAx6KyJmYH2d_1.4.F5.opExtrude","SWEPT_FACE",FACE,{"disambiguationData":[OSD([sQuery(id+"F4.wireOp",EDGE,"E6.right")])]})});
            var Q108;
            Q108=makeQuery(id+"FbWcAx6KyJmYH2d_1.4.F5.boolean.opBoolean","COPY",FACE,{"derivedFrom":makeQuery(id+"FbWcAx6KyJmYH2d_1.4.F5.opExtrude","SWEPT_FACE",FACE,{"disambiguationData":[OSD([sQuery(id+"F4.wireOp",EDGE,"E6.left")])]})});
            var Q109;
            Q109=makeQuery(id+"FbWcAx6KyJmYH2d_1.4.F5.boolean.opBoolean","COPY",FACE,{"derivedFrom":makeQuery(id+"FbWcAx6KyJmYH2d_1.4.F5.opExtrude","SWEPT_FACE",FACE,{"disambiguationData":[OSD([sQuery(id+"F4.wireOp",EDGE,"E6.bottom")])]})});
            var Q110;
            Q110=makeQuery(id+"FbWcAx6KyJmYH2d_1.2.F5.boolean.opBoolean","COPY",FACE,{"derivedFrom":makeQuery(id+"FbWcAx6KyJmYH2d_1.2.F5.opExtrude","SWEPT_FACE",FACE,{"disambiguationData":[OSD([sQuery(id+"F4.wireOp",EDGE,"E6.left")])]})});
            var Q111;
            Q111=makeQuery(id+"FbWcAx6KyJmYH2d_1.3.F5.boolean.opBoolean","INTERSECT",EDGE,{"derivedFrom":[makeQuery(id+"F1.opRevolve","SWEPT_FACE",FACE,{"disambiguationData":[OSD([sQuery(id+"F0.wireOp",EDGE,"E4")])]}),makeQuery(id+"FbWcAx6KyJmYH2d_1.3.F5.opExtrude","SWEPT_FACE",FACE,{"disambiguationData":[OSD([sQuery(id+"F4.wireOp",EDGE,"E6.bottom")])]})]});
            var Q112;
            Q112=makeQuery(id+"FbWcAx6KyJmYH2d_1.3.F5.boolean.opBoolean","COPY",FACE,{"derivedFrom":makeQuery(id+"FbWcAx6KyJmYH2d_1.3.F5.opExtrude","SWEPT_FACE",FACE,{"disambiguationData":[OSD([sQuery(id+"F4.wireOp",EDGE,"E8.filletArc")])]})});
            var Q113;
            Q113=makeQuery(id+"FbWcAx6KyJmYH2d_1.2.F5.boolean.opBoolean","COPY",FACE,{"derivedFrom":makeQuery(id+"FbWcAx6KyJmYH2d_1.2.F5.opExtrude","SWEPT_FACE",FACE,{"disambiguationData":[OSD([sQuery(id+"F4.wireOp",EDGE,"E7.filletArc")])]})});
            var Q114;
            Q114=makeQuery(id+"FbWcAx6KyJmYH2d_1.5.F5.boolean.opBoolean","INTERSECT",EDGE,{"derivedFrom":[makeQuery(id+"F2.opShell","OFFSET_FACE",FACE,{"disambiguationData":[OSD([sQuery(id+"F0.wireOp",EDGE,"E4")])]}),makeQuery(id+"FbWcAx6KyJmYH2d_1.5.F5.opExtrude","SWEPT_FACE",FACE,{"disambiguationData":[OSD([sQuery(id+"F4.wireOp",EDGE,"E6.left")])]})]});
            var Q115;
            Q115=makeQuery(id+"FbWcAx6KyJmYH2d_1.3.F5.boolean.opBoolean","INTERSECT",EDGE,{"derivedFrom":[makeQuery(id+"F1.opRevolve","SWEPT_FACE",FACE,{"disambiguationData":[OSD([sQuery(id+"F0.wireOp",EDGE,"E4")])]}),makeQuery(id+"FbWcAx6KyJmYH2d_1.3.F5.opExtrude","SWEPT_FACE",FACE,{"disambiguationData":[OSD([sQuery(id+"F4.wireOp",EDGE,"E6.left")])]})]});
            var Q116;
            Q116=makeQuery(id+"FbWcAx6KyJmYH2d_1.3.F5.boolean.opBoolean","COPY",FACE,{"derivedFrom":makeQuery(id+"FbWcAx6KyJmYH2d_1.3.F5.opExtrude","SWEPT_FACE",FACE,{"disambiguationData":[OSD([sQuery(id+"F4.wireOp",EDGE,"E6.right")])]})});
            var Q117;
            Q117=makeQuery(id+"FbWcAx6KyJmYH2d_1.3.F5.boolean.opBoolean","COPY",FACE,{"derivedFrom":makeQuery(id+"FbWcAx6KyJmYH2d_1.3.F5.opExtrude","SWEPT_FACE",FACE,{"disambiguationData":[OSD([sQuery(id+"F4.wireOp",EDGE,"E7.filletArc")])]})});
            var Q118;
            Q118=makeQuery(id+"FbWcAx6KyJmYH2d_1.3.F5.boolean.opBoolean","INTERSECT",EDGE,{"derivedFrom":[makeQuery(id+"F2.opShell","OFFSET_FACE",FACE,{"disambiguationData":[OSD([sQuery(id+"F0.wireOp",EDGE,"E4")])]}),makeQuery(id+"FbWcAx6KyJmYH2d_1.3.F5.opExtrude","SWEPT_FACE",FACE,{"disambiguationData":[OSD([sQuery(id+"F4.wireOp",EDGE,"E6.bottom")])]})]});
            var Q119;
            Q119=makeQuery(id+"FbWcAx6KyJmYH2d_1.3.F5.boolean.opBoolean","COPY",FACE,{"derivedFrom":makeQuery(id+"FbWcAx6KyJmYH2d_1.3.F5.opExtrude","SWEPT_FACE",FACE,{"disambiguationData":[OSD([sQuery(id+"F4.wireOp",EDGE,"E9.filletArc")])]})});
            var Q120;
            Q120=makeQuery(id+"F2.opShell","OFFSET_FACE",FACE,{"disambiguationData":[OSD([sQuery(id+"F0.wireOp",EDGE,"E2")])]});
            var Q121;
            Q121=makeQuery(id+"FbWcAx6KyJmYH2d_1.5.F5.boolean.opBoolean","COPY",EDGE,{"derivedFrom":makeQuery(id+"FbWcAx6KyJmYH2d_1.5.F5.opExtrude","SWEPT_EDGE",EDGE,{"disambiguationData":[OSD([sQuery(id+"F4.wireOp",EDGE,"E6.bottom"),sQuery(id+"F4.wireOp",EDGE,"E8.filletArc")])]})});
            var Q122;
            Q122=makeQuery(id+"FbWcAx6KyJmYH2d_1.1.F5.boolean.opBoolean","INTERSECT",EDGE,{"derivedFrom":[makeQuery(id+"F2.opShell","OFFSET_FACE",FACE,{"disambiguationData":[OSD([sQuery(id+"F0.wireOp",EDGE,"E4")])]}),makeQuery(id+"FbWcAx6KyJmYH2d_1.1.F5.opExtrude","SWEPT_FACE",FACE,{"disambiguationData":[OSD([sQuery(id+"F4.wireOp",EDGE,"E6.top")])]})]});
            var Q123;
            Q123=makeQuery(id+"FbWcAx6KyJmYH2d_1.2.F5.boolean.opBoolean","INTERSECT",EDGE,{"derivedFrom":[makeQuery(id+"F2.opShell","OFFSET_FACE",FACE,{"disambiguationData":[OSD([sQuery(id+"F0.wireOp",EDGE,"E4")])]}),makeQuery(id+"FbWcAx6KyJmYH2d_1.2.F5.opExtrude","SWEPT_FACE",FACE,{"disambiguationData":[OSD([sQuery(id+"F4.wireOp",EDGE,"E6.left")])]})]});
            var Q124;
            Q124=makeQuery(id+"FbWcAx6KyJmYH2d_1.2.F5.boolean.opBoolean","COPY",EDGE,{"derivedFrom":makeQuery(id+"FbWcAx6KyJmYH2d_1.2.F5.opExtrude","SWEPT_EDGE",EDGE,{"disambiguationData":[OSD([sQuery(id+"F4.wireOp",EDGE,"E6.bottom"),sQuery(id+"F4.wireOp",EDGE,"E8.filletArc")])]})});
            var Q125;
            {var subQ0=sQuery(id+"F0.wireOp",EDGE,"E2");Q125=makeQuery(id+"F3.opFillet","BLEND_EDGE",EDGE,{"blendedFrom":[makeQuery(id+"F1.opRevolve","SWEPT_EDGE",EDGE,{"disambiguationData":[OSD([subQ0,sQuery(id+"F0.wireOp",EDGE,"E4")])]}),makeQuery(id+"F1.opRevolve","SWEPT_FACE",FACE,{"disambiguationData":[OSD([subQ0])]})],"blendedInto":[makeQuery(id+"F1.opRevolve","SWEPT_FACE",FACE,{"disambiguationData":[OSD([subQ0])]})]});}
            var Q126;
            {var subQ0=sQuery(id+"F0.wireOp",EDGE,"E3");Q126=makeQuery(id+"F3.opFillet","BLEND_EDGE",EDGE,{"blendedFrom":[makeQuery(id+"F2.opShell","OFFSET_EDGE",EDGE,{"disambiguationData":[OSD([sQuery(id+"F0.wireOp",EDGE,"E1"),subQ0])]}),makeQuery(id+"F2.opShell","OFFSET_FACE",FACE,{"disambiguationData":[OSD([subQ0])]})],"blendedInto":[makeQuery(id+"F2.opShell","OFFSET_FACE",FACE,{"disambiguationData":[OSD([subQ0])]})]});}
            var Q127;
            Q127=makeQuery(id+"FbWcAx6KyJmYH2d_1.1.F5.boolean.opBoolean","COPY",FACE,{"derivedFrom":makeQuery(id+"FbWcAx6KyJmYH2d_1.1.F5.opExtrude","SWEPT_FACE",FACE,{"disambiguationData":[OSD([sQuery(id+"F4.wireOp",EDGE,"E10.filletArc")])]})});
            var Q128;
            {var subQ0=sQuery(id+"F0.wireOp",EDGE,"E3");Q128=makeQuery(id+"F3.opFillet","BLEND_EDGE",EDGE,{"blendedFrom":[makeQuery(id+"F2.opShell","OFFSET_EDGE",EDGE,{"disambiguationData":[OSD([subQ0,sQuery(id+"F0.wireOp",EDGE,"E4")])]}),makeQuery(id+"F2.opShell","OFFSET_FACE",FACE,{"disambiguationData":[OSD([subQ0])]})],"blendedInto":[makeQuery(id+"F2.opShell","OFFSET_FACE",FACE,{"disambiguationData":[OSD([subQ0])]})]});}
            var Q129;
            Q129=makeQuery(id+"FbWcAx6KyJmYH2d_1.3.F5.boolean.opBoolean","COPY",EDGE,{"derivedFrom":makeQuery(id+"FbWcAx6KyJmYH2d_1.3.F5.opExtrude","SWEPT_EDGE",EDGE,{"disambiguationData":[OSD([sQuery(id+"F4.wireOp",EDGE,"E6.left"),sQuery(id+"F4.wireOp",EDGE,"E9.filletArc")])]})});
            var Q130;
            Q130=makeQuery(id+"FbWcAx6KyJmYH2d_1.2.F5.boolean.opBoolean","COPY",FACE,{"derivedFrom":makeQuery(id+"FbWcAx6KyJmYH2d_1.2.F5.opExtrude","SWEPT_FACE",FACE,{"disambiguationData":[OSD([sQuery(id+"F4.wireOp",EDGE,"E6.top")])]})});
            var Q131;
            Q131=makeQuery(id+"FbWcAx6KyJmYH2d_1.2.F5.boolean.opBoolean","COPY",EDGE,{"derivedFrom":makeQuery(id+"FbWcAx6KyJmYH2d_1.2.F5.opExtrude","SWEPT_EDGE",EDGE,{"disambiguationData":[OSD([sQuery(id+"F4.wireOp",EDGE,"E6.top"),sQuery(id+"F4.wireOp",EDGE,"E10.filletArc")])]})});
            var Q132;
            Q132=makeQuery(id+"FbWcAx6KyJmYH2d_1.2.F5.boolean.opBoolean","COPY",EDGE,{"derivedFrom":makeQuery(id+"FbWcAx6KyJmYH2d_1.2.F5.opExtrude","SWEPT_EDGE",EDGE,{"disambiguationData":[OSD([sQuery(id+"F4.wireOp",EDGE,"E6.right"),sQuery(id+"F4.wireOp",EDGE,"E7.filletArc")])]})});
            var Q133;
            Q133=makeQuery(id+"FbWcAx6KyJmYH2d_1.2.F5.boolean.opBoolean","COPY",EDGE,{"derivedFrom":makeQuery(id+"FbWcAx6KyJmYH2d_1.2.F5.opExtrude","SWEPT_EDGE",EDGE,{"disambiguationData":[OSD([sQuery(id+"F4.wireOp",EDGE,"E6.left"),sQuery(id+"F4.wireOp",EDGE,"E9.filletArc")])]})});
            var Q134;
            Q134=makeQuery(id+"FbWcAx6KyJmYH2d_1.3.F5.boolean.opBoolean","COPY",EDGE,{"derivedFrom":makeQuery(id+"FbWcAx6KyJmYH2d_1.3.F5.opExtrude","SWEPT_EDGE",EDGE,{"disambiguationData":[OSD([sQuery(id+"F4.wireOp",EDGE,"E6.top"),sQuery(id+"F4.wireOp",EDGE,"E9.filletArc")])]})});
            var Q135;
            Q135=makeQuery(id+"F1.opRevolve","SWEPT_FACE",FACE,{"disambiguationData":[OSD([sQuery(id+"F0.wireOp",EDGE,"E2")])]});
            var Q136;
            {var subQ0=sQuery(id+"F0.wireOp",EDGE,"E4");var subQ1=sQuery(id+"F0.wireOp",EDGE,"E3");Q136=makeQuery(id+"F3.opFillet","BLEND_FACE",FACE,{"disambiguationData":[OSD([subQ1,subQ0]),TDD([makeQuery(id+"F2.opShell","OFFSET_EDGE",EDGE,{"disambiguationData":[OSD([subQ1,subQ0])]})])]});}
            var Q137;
            {var subQ0=sQuery(id+"F0.wireOp",EDGE,"E2");Q137=makeQuery(id+"F3.opFillet","BLEND_EDGE",EDGE,{"blendedFrom":[makeQuery(id+"F1.opRevolve","SWEPT_EDGE",EDGE,{"disambiguationData":[OSD([sQuery(id+"F0.wireOp",EDGE,"E1"),subQ0])]}),makeQuery(id+"F1.opRevolve","SWEPT_FACE",FACE,{"disambiguationData":[OSD([subQ0])]})],"blendedInto":[makeQuery(id+"F1.opRevolve","SWEPT_FACE",FACE,{"disambiguationData":[OSD([subQ0])]})]});}
            var Q138;
            Q138=makeQuery(id+"F2.opShell","OFFSET_FACE",FACE,{"disambiguationData":[OSD([sQuery(id+"F0.wireOp",EDGE,"E3")])]});
            var Q139;
            {var subQ0=sQuery(id+"F0.wireOp",EDGE,"E4");Q139=makeQuery(id+"F3.opFillet","BLEND_EDGE",EDGE,{"blendedFrom":[makeQuery(id+"F2.opShell","OFFSET_EDGE",EDGE,{"disambiguationData":[OSD([sQuery(id+"F0.wireOp",EDGE,"E3"),subQ0])]}),makeQuery(id+"F2.opShell","OFFSET_FACE",FACE,{"disambiguationData":[OSD([subQ0])]})],"blendedInto":[makeQuery(id+"F2.opShell","OFFSET_FACE",FACE,{"disambiguationData":[OSD([subQ0])]})]});}
            var Q140;
            Q140=makeQuery(id+"FbWcAx6KyJmYH2d_1.3.F5.boolean.opBoolean","COPY",EDGE,{"derivedFrom":makeQuery(id+"FbWcAx6KyJmYH2d_1.3.F5.opExtrude","SWEPT_EDGE",EDGE,{"disambiguationData":[OSD([sQuery(id+"F4.wireOp",EDGE,"E6.bottom"),sQuery(id+"F4.wireOp",EDGE,"E7.filletArc")])]})});
            var Q141;
            Q141=makeQuery(id+"FbWcAx6KyJmYH2d_1.1.F5.boolean.opBoolean","COPY",EDGE,{"derivedFrom":makeQuery(id+"FbWcAx6KyJmYH2d_1.1.F5.opExtrude","SWEPT_EDGE",EDGE,{"disambiguationData":[OSD([sQuery(id+"F4.wireOp",EDGE,"E6.top"),sQuery(id+"F4.wireOp",EDGE,"E9.filletArc")])]})});
            var Q142;
            Q142=makeQuery(id+"FbWcAx6KyJmYH2d_1.1.F5.boolean.opBoolean","COPY",EDGE,{"derivedFrom":makeQuery(id+"FbWcAx6KyJmYH2d_1.1.F5.opExtrude","SWEPT_EDGE",EDGE,{"disambiguationData":[OSD([sQuery(id+"F4.wireOp",EDGE,"E6.left"),sQuery(id+"F4.wireOp",EDGE,"E8.filletArc")])]})});
            var Q143;
            Q143=makeQuery(id+"FbWcAx6KyJmYH2d_1.4.F5.boolean.opBoolean","COPY",EDGE,{"derivedFrom":makeQuery(id+"FbWcAx6KyJmYH2d_1.4.F5.opExtrude","SWEPT_EDGE",EDGE,{"disambiguationData":[OSD([sQuery(id+"F4.wireOp",EDGE,"E6.bottom"),sQuery(id+"F4.wireOp",EDGE,"E8.filletArc")])]})});
            var Q144;
            Q144=makeQuery(id+"FbWcAx6KyJmYH2d_1.1.F5.boolean.opBoolean","COPY",EDGE,{"derivedFrom":makeQuery(id+"FbWcAx6KyJmYH2d_1.1.F5.opExtrude","SWEPT_EDGE",EDGE,{"disambiguationData":[OSD([sQuery(id+"F4.wireOp",EDGE,"E6.left"),sQuery(id+"F4.wireOp",EDGE,"E9.filletArc")])]})});
            var Q145;
            Q145=makeQuery(id+"FbWcAx6KyJmYH2d_1.1.F5.boolean.opBoolean","COPY",FACE,{"derivedFrom":makeQuery(id+"FbWcAx6KyJmYH2d_1.1.F5.opExtrude","SWEPT_FACE",FACE,{"disambiguationData":[OSD([sQuery(id+"F4.wireOp",EDGE,"E8.filletArc")])]})});
            var Q146;
            Q146=makeQuery(id+"FbWcAx6KyJmYH2d_1.1.F5.boolean.opBoolean","INTERSECT",EDGE,{"derivedFrom":[makeQuery(id+"F2.opShell","OFFSET_FACE",FACE,{"disambiguationData":[OSD([sQuery(id+"F0.wireOp",EDGE,"E4")])]}),makeQuery(id+"FbWcAx6KyJmYH2d_1.1.F5.opExtrude","SWEPT_FACE",FACE,{"disambiguationData":[OSD([sQuery(id+"F4.wireOp",EDGE,"E6.bottom")])]})]});
            var Q147;
            Q147=makeQuery(id+"FbWcAx6KyJmYH2d_1.1.F5.boolean.opBoolean","COPY",EDGE,{"derivedFrom":makeQuery(id+"FbWcAx6KyJmYH2d_1.1.F5.opExtrude","SWEPT_EDGE",EDGE,{"disambiguationData":[OSD([sQuery(id+"F4.wireOp",EDGE,"E6.right"),sQuery(id+"F4.wireOp",EDGE,"E7.filletArc")])]})});
            var Q148;
            Q148=makeQuery(id+"FbWcAx6KyJmYH2d_1.2.F5.boolean.opBoolean","COPY",EDGE,{"derivedFrom":makeQuery(id+"FbWcAx6KyJmYH2d_1.2.F5.opExtrude","SWEPT_EDGE",EDGE,{"disambiguationData":[OSD([sQuery(id+"F4.wireOp",EDGE,"E6.bottom"),sQuery(id+"F4.wireOp",EDGE,"E7.filletArc")])]})});
            var Q149;
            Q149=makeQuery(id+"FbWcAx6KyJmYH2d_1.2.F5.boolean.opBoolean","INTERSECT",EDGE,{"derivedFrom":[makeQuery(id+"F2.opShell","OFFSET_FACE",FACE,{"disambiguationData":[OSD([sQuery(id+"F0.wireOp",EDGE,"E4")])]}),makeQuery(id+"FbWcAx6KyJmYH2d_1.2.F5.opExtrude","SWEPT_FACE",FACE,{"disambiguationData":[OSD([sQuery(id+"F4.wireOp",EDGE,"E6.top")])]})]});
            var Q150;
            Q150=makeQuery(id+"FbWcAx6KyJmYH2d_1.3.F5.boolean.opBoolean","INTERSECT",EDGE,{"derivedFrom":[makeQuery(id+"F2.opShell","OFFSET_FACE",FACE,{"disambiguationData":[OSD([sQuery(id+"F0.wireOp",EDGE,"E4")])]}),makeQuery(id+"FbWcAx6KyJmYH2d_1.3.F5.opExtrude","SWEPT_FACE",FACE,{"disambiguationData":[OSD([sQuery(id+"F4.wireOp",EDGE,"E6.right")])]})]});
            var Q151;
            Q151=makeQuery(id+"FbWcAx6KyJmYH2d_1.3.F5.boolean.opBoolean","COPY",EDGE,{"derivedFrom":makeQuery(id+"FbWcAx6KyJmYH2d_1.3.F5.opExtrude","SWEPT_EDGE",EDGE,{"disambiguationData":[OSD([sQuery(id+"F4.wireOp",EDGE,"E6.bottom"),sQuery(id+"F4.wireOp",EDGE,"E8.filletArc")])]})});
            var Q152;
            Q152=makeQuery(id+"FbWcAx6KyJmYH2d_1.3.F5.boolean.opBoolean","COPY",EDGE,{"derivedFrom":makeQuery(id+"FbWcAx6KyJmYH2d_1.3.F5.opExtrude","SWEPT_EDGE",EDGE,{"disambiguationData":[OSD([sQuery(id+"F4.wireOp",EDGE,"E6.top"),sQuery(id+"F4.wireOp",EDGE,"E10.filletArc")])]})});
            var Q153;
            Q153=makeQuery(id+"FbWcAx6KyJmYH2d_1.4.F5.boolean.opBoolean","COPY",EDGE,{"derivedFrom":makeQuery(id+"FbWcAx6KyJmYH2d_1.4.F5.opExtrude","SWEPT_EDGE",EDGE,{"disambiguationData":[OSD([sQuery(id+"F4.wireOp",EDGE,"E6.bottom"),sQuery(id+"F4.wireOp",EDGE,"E7.filletArc")])]})});
            var Q154;
            Q154=makeQuery(id+"FbWcAx6KyJmYH2d_1.1.F5.boolean.opBoolean","COPY",EDGE,{"derivedFrom":makeQuery(id+"FbWcAx6KyJmYH2d_1.1.F5.opExtrude","SWEPT_EDGE",EDGE,{"disambiguationData":[OSD([sQuery(id+"F4.wireOp",EDGE,"E6.bottom"),sQuery(id+"F4.wireOp",EDGE,"E7.filletArc")])]})});
            var Q155;
            Q155=makeQuery(id+"FbWcAx6KyJmYH2d_1.1.F5.boolean.opBoolean","COPY",FACE,{"derivedFrom":makeQuery(id+"FbWcAx6KyJmYH2d_1.1.F5.opExtrude","SWEPT_FACE",FACE,{"disambiguationData":[OSD([sQuery(id+"F4.wireOp",EDGE,"E6.top")])]})});
            var Q156;
            Q156=makeQuery(id+"FbWcAx6KyJmYH2d_1.1.F5.boolean.opBoolean","INTERSECT",EDGE,{"derivedFrom":[makeQuery(id+"F2.opShell","OFFSET_FACE",FACE,{"disambiguationData":[OSD([sQuery(id+"F0.wireOp",EDGE,"E4")])]}),makeQuery(id+"FbWcAx6KyJmYH2d_1.1.F5.opExtrude","SWEPT_FACE",FACE,{"disambiguationData":[OSD([sQuery(id+"F4.wireOp",EDGE,"E6.right")])]})]});
            var Q157;
            Q157=makeQuery(id+"F5.boolean.opBoolean","INTERSECT",EDGE,{"derivedFrom":[makeQuery(id+"F1.opRevolve","SWEPT_FACE",FACE,{"disambiguationData":[OSD([sQuery(id+"F0.wireOp",EDGE,"E4")])]}),makeQuery(id+"F5.opExtrude","SWEPT_FACE",FACE,{"disambiguationData":[OSD([sQuery(id+"F4.wireOp",EDGE,"E6.top")])]})]});
            var Q158;
            Q158=makeQuery(id+"F5.boolean.opBoolean","COPY",EDGE,{"derivedFrom":makeQuery(id+"F5.opExtrude","SWEPT_EDGE",EDGE,{"disambiguationData":[OSD([sQuery(id+"F4.wireOp",EDGE,"E6.right"),sQuery(id+"F4.wireOp",EDGE,"E10.filletArc")])]})});
            var Q159;
            Q159=makeQuery(id+"F5.boolean.opBoolean","COPY",FACE,{"derivedFrom":makeQuery(id+"F5.opExtrude","SWEPT_FACE",FACE,{"disambiguationData":[OSD([sQuery(id+"F4.wireOp",EDGE,"E9.filletArc")])]})});
            var Q160;
            Q160=makeQuery(id+"F5.boolean.opBoolean","COPY",EDGE,{"derivedFrom":makeQuery(id+"F5.opExtrude","SWEPT_EDGE",EDGE,{"disambiguationData":[OSD([sQuery(id+"F4.wireOp",EDGE,"E6.right"),sQuery(id+"F4.wireOp",EDGE,"E7.filletArc")])]})});
            var Q161;
            Q161=makeQuery(id+"F5.boolean.opBoolean","COPY",FACE,{"derivedFrom":makeQuery(id+"F5.opExtrude","SWEPT_FACE",FACE,{"disambiguationData":[OSD([sQuery(id+"F4.wireOp",EDGE,"E8.filletArc")])]})});
            var Q162;
            Q162=makeQuery(id+"F5.boolean.opBoolean","COPY",FACE,{"derivedFrom":makeQuery(id+"F5.opExtrude","SWEPT_FACE",FACE,{"disambiguationData":[OSD([sQuery(id+"F4.wireOp",EDGE,"E6.left")])]})});
            var Q163;
            Q163=makeQuery(id+"F5.boolean.opBoolean","COPY",EDGE,{"derivedFrom":makeQuery(id+"F5.opExtrude","SWEPT_EDGE",EDGE,{"disambiguationData":[OSD([sQuery(id+"F4.wireOp",EDGE,"E6.bottom"),sQuery(id+"F4.wireOp",EDGE,"E7.filletArc")])]})});
            var Q164;
            Q164=makeQuery(id+"F5.boolean.opBoolean","COPY",FACE,{"derivedFrom":makeQuery(id+"F5.opExtrude","SWEPT_FACE",FACE,{"disambiguationData":[OSD([sQuery(id+"F4.wireOp",EDGE,"E6.top")])]})});
            var Q165;
            Q165=makeQuery(id+"FbWcAx6KyJmYH2d_1.6.F5.boolean.opBoolean","INTERSECT",EDGE,{"derivedFrom":[makeQuery(id+"F2.opShell","OFFSET_FACE",FACE,{"disambiguationData":[OSD([sQuery(id+"F0.wireOp",EDGE,"E4")])]}),makeQuery(id+"FbWcAx6KyJmYH2d_1.6.F5.opExtrude","SWEPT_FACE",FACE,{"disambiguationData":[OSD([sQuery(id+"F4.wireOp",EDGE,"E10.filletArc")])]})]});
            var Q166;
            Q166=makeQuery(id+"FbWcAx6KyJmYH2d_1.6.F5.boolean.opBoolean","INTERSECT",EDGE,{"derivedFrom":[makeQuery(id+"F1.opRevolve","SWEPT_FACE",FACE,{"disambiguationData":[OSD([sQuery(id+"F0.wireOp",EDGE,"E4")])]}),makeQuery(id+"FbWcAx6KyJmYH2d_1.6.F5.opExtrude","SWEPT_FACE",FACE,{"disambiguationData":[OSD([sQuery(id+"F4.wireOp",EDGE,"E10.filletArc")])]})]});
            var Q167;
            Q167=makeQuery(id+"FbWcAx6KyJmYH2d_1.6.F5.boolean.opBoolean","INTERSECT",EDGE,{"derivedFrom":[makeQuery(id+"F1.opRevolve","SWEPT_FACE",FACE,{"disambiguationData":[OSD([sQuery(id+"F0.wireOp",EDGE,"E4")])]}),makeQuery(id+"FbWcAx6KyJmYH2d_1.6.F5.opExtrude","SWEPT_FACE",FACE,{"disambiguationData":[OSD([sQuery(id+"F4.wireOp",EDGE,"E9.filletArc")])]})]});
            var Q168;
            Q168=makeQuery(id+"FbWcAx6KyJmYH2d_1.5.F5.boolean.opBoolean","INTERSECT",EDGE,{"derivedFrom":[makeQuery(id+"F1.opRevolve","SWEPT_FACE",FACE,{"disambiguationData":[OSD([sQuery(id+"F0.wireOp",EDGE,"E4")])]}),makeQuery(id+"FbWcAx6KyJmYH2d_1.5.F5.opExtrude","SWEPT_FACE",FACE,{"disambiguationData":[OSD([sQuery(id+"F4.wireOp",EDGE,"E10.filletArc")])]})]});
            var Q169;
            Q169=makeQuery(id+"FbWcAx6KyJmYH2d_1.4.F5.boolean.opBoolean","INTERSECT",EDGE,{"derivedFrom":[makeQuery(id+"F2.opShell","OFFSET_FACE",FACE,{"disambiguationData":[OSD([sQuery(id+"F0.wireOp",EDGE,"E4")])]}),makeQuery(id+"FbWcAx6KyJmYH2d_1.4.F5.opExtrude","SWEPT_FACE",FACE,{"disambiguationData":[OSD([sQuery(id+"F4.wireOp",EDGE,"E10.filletArc")])]})]});
            var Q170;
            Q170=makeQuery(id+"FbWcAx6KyJmYH2d_1.4.F5.boolean.opBoolean","INTERSECT",EDGE,{"derivedFrom":[makeQuery(id+"F2.opShell","OFFSET_FACE",FACE,{"disambiguationData":[OSD([sQuery(id+"F0.wireOp",EDGE,"E4")])]}),makeQuery(id+"FbWcAx6KyJmYH2d_1.4.F5.opExtrude","SWEPT_FACE",FACE,{"disambiguationData":[OSD([sQuery(id+"F4.wireOp",EDGE,"E8.filletArc")])]})]});
            var Q171;
            Q171=makeQuery(id+"FbWcAx6KyJmYH2d_1.4.F5.boolean.opBoolean","INTERSECT",EDGE,{"derivedFrom":[makeQuery(id+"F1.opRevolve","SWEPT_FACE",FACE,{"disambiguationData":[OSD([sQuery(id+"F0.wireOp",EDGE,"E4")])]}),makeQuery(id+"FbWcAx6KyJmYH2d_1.4.F5.opExtrude","SWEPT_FACE",FACE,{"disambiguationData":[OSD([sQuery(id+"F4.wireOp",EDGE,"E9.filletArc")])]})]});
            var Q172;
            Q172=makeQuery(id+"FbWcAx6KyJmYH2d_1.3.F5.boolean.opBoolean","INTERSECT",EDGE,{"derivedFrom":[makeQuery(id+"F2.opShell","OFFSET_FACE",FACE,{"disambiguationData":[OSD([sQuery(id+"F0.wireOp",EDGE,"E4")])]}),makeQuery(id+"FbWcAx6KyJmYH2d_1.3.F5.opExtrude","SWEPT_FACE",FACE,{"disambiguationData":[OSD([sQuery(id+"F4.wireOp",EDGE,"E10.filletArc")])]})]});
            var Q173;
            Q173=makeQuery(id+"FbWcAx6KyJmYH2d_1.3.F5.boolean.opBoolean","INTERSECT",EDGE,{"derivedFrom":[makeQuery(id+"F2.opShell","OFFSET_FACE",FACE,{"disambiguationData":[OSD([sQuery(id+"F0.wireOp",EDGE,"E4")])]}),makeQuery(id+"FbWcAx6KyJmYH2d_1.3.F5.opExtrude","SWEPT_FACE",FACE,{"disambiguationData":[OSD([sQuery(id+"F4.wireOp",EDGE,"E9.filletArc")])]})]});
            var Q174;
            Q174=makeQuery(id+"FbWcAx6KyJmYH2d_1.3.F5.boolean.opBoolean","INTERSECT",EDGE,{"derivedFrom":[makeQuery(id+"F1.opRevolve","SWEPT_FACE",FACE,{"disambiguationData":[OSD([sQuery(id+"F0.wireOp",EDGE,"E4")])]}),makeQuery(id+"FbWcAx6KyJmYH2d_1.3.F5.opExtrude","SWEPT_FACE",FACE,{"disambiguationData":[OSD([sQuery(id+"F4.wireOp",EDGE,"E8.filletArc")])]})]});
            var Q175;
            Q175=makeQuery(id+"FbWcAx6KyJmYH2d_1.3.F5.boolean.opBoolean","INTERSECT",EDGE,{"derivedFrom":[makeQuery(id+"F2.opShell","OFFSET_FACE",FACE,{"disambiguationData":[OSD([sQuery(id+"F0.wireOp",EDGE,"E4")])]}),makeQuery(id+"FbWcAx6KyJmYH2d_1.3.F5.opExtrude","SWEPT_FACE",FACE,{"disambiguationData":[OSD([sQuery(id+"F4.wireOp",EDGE,"E7.filletArc")])]})]});
            var Q176;
            Q176=makeQuery(id+"FbWcAx6KyJmYH2d_1.2.F5.boolean.opBoolean","INTERSECT",EDGE,{"derivedFrom":[makeQuery(id+"F2.opShell","OFFSET_FACE",FACE,{"disambiguationData":[OSD([sQuery(id+"F0.wireOp",EDGE,"E4")])]}),makeQuery(id+"FbWcAx6KyJmYH2d_1.2.F5.opExtrude","SWEPT_FACE",FACE,{"disambiguationData":[OSD([sQuery(id+"F4.wireOp",EDGE,"E9.filletArc")])]})]});
            var Q177;
            Q177=makeQuery(id+"FbWcAx6KyJmYH2d_1.1.F5.boolean.opBoolean","INTERSECT",EDGE,{"derivedFrom":[makeQuery(id+"F2.opShell","OFFSET_FACE",FACE,{"disambiguationData":[OSD([sQuery(id+"F0.wireOp",EDGE,"E4")])]}),makeQuery(id+"FbWcAx6KyJmYH2d_1.1.F5.opExtrude","SWEPT_FACE",FACE,{"disambiguationData":[OSD([sQuery(id+"F4.wireOp",EDGE,"E9.filletArc")])]})]});
            var Q178;
            Q178=makeQuery(id+"FbWcAx6KyJmYH2d_1.2.F5.boolean.opBoolean","INTERSECT",EDGE,{"derivedFrom":[makeQuery(id+"F2.opShell","OFFSET_FACE",FACE,{"disambiguationData":[OSD([sQuery(id+"F0.wireOp",EDGE,"E4")])]}),makeQuery(id+"FbWcAx6KyJmYH2d_1.2.F5.opExtrude","SWEPT_FACE",FACE,{"disambiguationData":[OSD([sQuery(id+"F4.wireOp",EDGE,"E8.filletArc")])]})]});
            var Q179;
            Q179=makeQuery(id+"FbWcAx6KyJmYH2d_1.1.F5.boolean.opBoolean","INTERSECT",EDGE,{"derivedFrom":[makeQuery(id+"F1.opRevolve","SWEPT_FACE",FACE,{"disambiguationData":[OSD([sQuery(id+"F0.wireOp",EDGE,"E4")])]}),makeQuery(id+"FbWcAx6KyJmYH2d_1.1.F5.opExtrude","SWEPT_FACE",FACE,{"disambiguationData":[OSD([sQuery(id+"F4.wireOp",EDGE,"E10.filletArc")])]})]});
            var Q180;
            Q180=makeQuery(id+"FbWcAx6KyJmYH2d_1.1.F5.boolean.opBoolean","INTERSECT",EDGE,{"derivedFrom":[makeQuery(id+"F2.opShell","OFFSET_FACE",FACE,{"disambiguationData":[OSD([sQuery(id+"F0.wireOp",EDGE,"E4")])]}),makeQuery(id+"FbWcAx6KyJmYH2d_1.1.F5.opExtrude","SWEPT_FACE",FACE,{"disambiguationData":[OSD([sQuery(id+"F4.wireOp",EDGE,"E8.filletArc")])]})]});
            var Q181;
            Q181=makeQuery(id+"F5.boolean.opBoolean","INTERSECT",EDGE,{"derivedFrom":[makeQuery(id+"F2.opShell","OFFSET_FACE",FACE,{"disambiguationData":[OSD([sQuery(id+"F0.wireOp",EDGE,"E4")])]}),makeQuery(id+"F5.opExtrude","SWEPT_FACE",FACE,{"disambiguationData":[OSD([sQuery(id+"F4.wireOp",EDGE,"E10.filletArc")])]})]});
            var Q182;
            Q182=makeQuery(id+"F5.boolean.opBoolean","INTERSECT",EDGE,{"derivedFrom":[makeQuery(id+"F1.opRevolve","SWEPT_FACE",FACE,{"disambiguationData":[OSD([sQuery(id+"F0.wireOp",EDGE,"E4")])]}),makeQuery(id+"F5.opExtrude","SWEPT_FACE",FACE,{"disambiguationData":[OSD([sQuery(id+"F4.wireOp",EDGE,"E9.filletArc")])]})]});
            var Q183;
            Q183=makeQuery(id+"FbWcAx6KyJmYH2d_1.6.F5.boolean.opBoolean","INTERSECT",EDGE,{"derivedFrom":[makeQuery(id+"F1.opRevolve","SWEPT_FACE",FACE,{"disambiguationData":[OSD([sQuery(id+"F0.wireOp",EDGE,"E4")])]}),makeQuery(id+"FbWcAx6KyJmYH2d_1.6.F5.opExtrude","SWEPT_FACE",FACE,{"disambiguationData":[OSD([sQuery(id+"F4.wireOp",EDGE,"E6.top")])]})]});
            var Q184;
            Q184=makeQuery(id+"FbWcAx6KyJmYH2d_1.6.F5.boolean.opBoolean","COPY",EDGE,{"derivedFrom":makeQuery(id+"FbWcAx6KyJmYH2d_1.6.F5.opExtrude","SWEPT_EDGE",EDGE,{"disambiguationData":[OSD([sQuery(id+"F4.wireOp",EDGE,"E6.left"),sQuery(id+"F4.wireOp",EDGE,"E8.filletArc")])]})});
            var Q185;
            Q185=makeQuery(id+"FbWcAx6KyJmYH2d_1.6.F5.boolean.opBoolean","COPY",EDGE,{"derivedFrom":makeQuery(id+"FbWcAx6KyJmYH2d_1.6.F5.opExtrude","SWEPT_EDGE",EDGE,{"disambiguationData":[OSD([sQuery(id+"F4.wireOp",EDGE,"E6.left"),sQuery(id+"F4.wireOp",EDGE,"E9.filletArc")])]})});
            var Q186;
            Q186=makeQuery(id+"FbWcAx6KyJmYH2d_1.6.F5.boolean.opBoolean","COPY",EDGE,{"derivedFrom":makeQuery(id+"FbWcAx6KyJmYH2d_1.6.F5.opExtrude","SWEPT_EDGE",EDGE,{"disambiguationData":[OSD([sQuery(id+"F4.wireOp",EDGE,"E6.bottom"),sQuery(id+"F4.wireOp",EDGE,"E7.filletArc")])]})});
            var Q187;
            Q187=makeQuery(id+"FbWcAx6KyJmYH2d_1.6.F5.boolean.opBoolean","COPY",FACE,{"derivedFrom":makeQuery(id+"FbWcAx6KyJmYH2d_1.6.F5.opExtrude","SWEPT_FACE",FACE,{"disambiguationData":[OSD([sQuery(id+"F4.wireOp",EDGE,"E6.top")])]})});
            var Q188;
            Q188=makeQuery(id+"FbWcAx6KyJmYH2d_1.6.F5.boolean.opBoolean","COPY",EDGE,{"derivedFrom":makeQuery(id+"FbWcAx6KyJmYH2d_1.6.F5.opExtrude","SWEPT_EDGE",EDGE,{"disambiguationData":[OSD([sQuery(id+"F4.wireOp",EDGE,"E6.bottom"),sQuery(id+"F4.wireOp",EDGE,"E8.filletArc")])]})});
            var Q189;
            Q189=makeQuery(id+"FbWcAx6KyJmYH2d_1.6.F5.boolean.opBoolean","INTERSECT",EDGE,{"derivedFrom":[makeQuery(id+"F1.opRevolve","SWEPT_FACE",FACE,{"disambiguationData":[OSD([sQuery(id+"F0.wireOp",EDGE,"E4")])]}),makeQuery(id+"FbWcAx6KyJmYH2d_1.6.F5.opExtrude","SWEPT_FACE",FACE,{"disambiguationData":[OSD([sQuery(id+"F4.wireOp",EDGE,"E6.right")])]})]});
            var Q190;
            Q190=makeQuery(id+"FbWcAx6KyJmYH2d_1.5.F5.boolean.opBoolean","INTERSECT",EDGE,{"derivedFrom":[makeQuery(id+"F1.opRevolve","SWEPT_FACE",FACE,{"disambiguationData":[OSD([sQuery(id+"F0.wireOp",EDGE,"E4")])]}),makeQuery(id+"FbWcAx6KyJmYH2d_1.5.F5.opExtrude","SWEPT_FACE",FACE,{"disambiguationData":[OSD([sQuery(id+"F4.wireOp",EDGE,"E6.top")])]})]});
            var Q191;
            Q191=makeQuery(id+"FbWcAx6KyJmYH2d_1.5.F5.boolean.opBoolean","INTERSECT",EDGE,{"derivedFrom":[makeQuery(id+"F2.opShell","OFFSET_FACE",FACE,{"disambiguationData":[OSD([sQuery(id+"F0.wireOp",EDGE,"E4")])]}),makeQuery(id+"FbWcAx6KyJmYH2d_1.5.F5.opExtrude","SWEPT_FACE",FACE,{"disambiguationData":[OSD([sQuery(id+"F4.wireOp",EDGE,"E6.bottom")])]})]});
            var Q192;
            Q192=makeQuery(id+"FbWcAx6KyJmYH2d_1.5.F5.boolean.opBoolean","INTERSECT",EDGE,{"derivedFrom":[makeQuery(id+"F1.opRevolve","SWEPT_FACE",FACE,{"disambiguationData":[OSD([sQuery(id+"F0.wireOp",EDGE,"E4")])]}),makeQuery(id+"FbWcAx6KyJmYH2d_1.5.F5.opExtrude","SWEPT_FACE",FACE,{"disambiguationData":[OSD([sQuery(id+"F4.wireOp",EDGE,"E6.bottom")])]})]});
            var Q193;
            Q193=makeQuery(id+"FbWcAx6KyJmYH2d_1.5.F5.boolean.opBoolean","COPY",FACE,{"derivedFrom":makeQuery(id+"FbWcAx6KyJmYH2d_1.5.F5.opExtrude","SWEPT_FACE",FACE,{"disambiguationData":[OSD([sQuery(id+"F4.wireOp",EDGE,"E10.filletArc")])]})});
            var Q194;
            Q194=makeQuery(id+"FbWcAx6KyJmYH2d_1.5.F5.boolean.opBoolean","COPY",EDGE,{"derivedFrom":makeQuery(id+"FbWcAx6KyJmYH2d_1.5.F5.opExtrude","SWEPT_EDGE",EDGE,{"disambiguationData":[OSD([sQuery(id+"F4.wireOp",EDGE,"E6.right"),sQuery(id+"F4.wireOp",EDGE,"E10.filletArc")])]})});
            var Q195;
            Q195=makeQuery(id+"FbWcAx6KyJmYH2d_1.5.F5.boolean.opBoolean","COPY",FACE,{"derivedFrom":makeQuery(id+"FbWcAx6KyJmYH2d_1.5.F5.opExtrude","SWEPT_FACE",FACE,{"disambiguationData":[OSD([sQuery(id+"F4.wireOp",EDGE,"E9.filletArc")])]})});
            var Q196;
            Q196=makeQuery(id+"FbWcAx6KyJmYH2d_1.5.F5.boolean.opBoolean","COPY",EDGE,{"derivedFrom":makeQuery(id+"FbWcAx6KyJmYH2d_1.5.F5.opExtrude","SWEPT_EDGE",EDGE,{"disambiguationData":[OSD([sQuery(id+"F4.wireOp",EDGE,"E6.right"),sQuery(id+"F4.wireOp",EDGE,"E7.filletArc")])]})});
            var Q197;
            Q197=makeQuery(id+"FbWcAx6KyJmYH2d_1.5.F5.boolean.opBoolean","COPY",EDGE,{"derivedFrom":makeQuery(id+"FbWcAx6KyJmYH2d_1.5.F5.opExtrude","SWEPT_EDGE",EDGE,{"disambiguationData":[OSD([sQuery(id+"F4.wireOp",EDGE,"E6.left"),sQuery(id+"F4.wireOp",EDGE,"E8.filletArc")])]})});
            var Q198;
            Q198=makeQuery(id+"FbWcAx6KyJmYH2d_1.5.F5.boolean.opBoolean","COPY",FACE,{"derivedFrom":makeQuery(id+"FbWcAx6KyJmYH2d_1.5.F5.opExtrude","SWEPT_FACE",FACE,{"disambiguationData":[OSD([sQuery(id+"F4.wireOp",EDGE,"E7.filletArc")])]})});
            var Q199;
            Q199=makeQuery(id+"FbWcAx6KyJmYH2d_1.5.F5.boolean.opBoolean","COPY",FACE,{"derivedFrom":makeQuery(id+"FbWcAx6KyJmYH2d_1.5.F5.opExtrude","SWEPT_FACE",FACE,{"disambiguationData":[OSD([sQuery(id+"F4.wireOp",EDGE,"E6.right")])]})});
            var Q200;
            Q200=makeQuery(id+"FbWcAx6KyJmYH2d_1.5.F5.boolean.opBoolean","COPY",FACE,{"derivedFrom":makeQuery(id+"FbWcAx6KyJmYH2d_1.5.F5.opExtrude","SWEPT_FACE",FACE,{"disambiguationData":[OSD([sQuery(id+"F4.wireOp",EDGE,"E6.top")])]})});
            var Q201;
            Q201=makeQuery(id+"FbWcAx6KyJmYH2d_1.5.F5.boolean.opBoolean","INTERSECT",EDGE,{"derivedFrom":[makeQuery(id+"F2.opShell","OFFSET_FACE",FACE,{"disambiguationData":[OSD([sQuery(id+"F0.wireOp",EDGE,"E4")])]}),makeQuery(id+"FbWcAx6KyJmYH2d_1.5.F5.opExtrude","SWEPT_FACE",FACE,{"disambiguationData":[OSD([sQuery(id+"F4.wireOp",EDGE,"E6.right")])]})]});
            var Q202;
            Q202=makeQuery(id+"FbWcAx6KyJmYH2d_1.5.F5.boolean.opBoolean","INTERSECT",EDGE,{"derivedFrom":[makeQuery(id+"F1.opRevolve","SWEPT_FACE",FACE,{"disambiguationData":[OSD([sQuery(id+"F0.wireOp",EDGE,"E4")])]}),makeQuery(id+"FbWcAx6KyJmYH2d_1.5.F5.opExtrude","SWEPT_FACE",FACE,{"disambiguationData":[OSD([sQuery(id+"F4.wireOp",EDGE,"E6.right")])]})]});
            var Q203;
            Q203=makeQuery(id+"FbWcAx6KyJmYH2d_1.4.F5.boolean.opBoolean","INTERSECT",EDGE,{"derivedFrom":[makeQuery(id+"F2.opShell","OFFSET_FACE",FACE,{"disambiguationData":[OSD([sQuery(id+"F0.wireOp",EDGE,"E4")])]}),makeQuery(id+"FbWcAx6KyJmYH2d_1.4.F5.opExtrude","SWEPT_FACE",FACE,{"disambiguationData":[OSD([sQuery(id+"F4.wireOp",EDGE,"E6.top")])]})]});
            var Q204;
            Q204=makeQuery(id+"FbWcAx6KyJmYH2d_1.4.F5.boolean.opBoolean","COPY",EDGE,{"derivedFrom":makeQuery(id+"FbWcAx6KyJmYH2d_1.4.F5.opExtrude","SWEPT_EDGE",EDGE,{"disambiguationData":[OSD([sQuery(id+"F4.wireOp",EDGE,"E6.right"),sQuery(id+"F4.wireOp",EDGE,"E10.filletArc")])]})});
            var Q205;
            Q205=makeQuery(id+"FbWcAx6KyJmYH2d_1.4.F5.boolean.opBoolean","COPY",FACE,{"derivedFrom":makeQuery(id+"FbWcAx6KyJmYH2d_1.4.F5.opExtrude","SWEPT_FACE",FACE,{"disambiguationData":[OSD([sQuery(id+"F4.wireOp",EDGE,"E9.filletArc")])]})});
            var Q206;
            Q206=makeQuery(id+"FbWcAx6KyJmYH2d_1.4.F5.boolean.opBoolean","COPY",FACE,{"derivedFrom":makeQuery(id+"FbWcAx6KyJmYH2d_1.4.F5.opExtrude","SWEPT_FACE",FACE,{"disambiguationData":[OSD([sQuery(id+"F4.wireOp",EDGE,"E7.filletArc")])]})});
            var Q207;
            Q207=makeQuery(id+"FbWcAx6KyJmYH2d_1.4.F5.boolean.opBoolean","COPY",EDGE,{"derivedFrom":makeQuery(id+"FbWcAx6KyJmYH2d_1.4.F5.opExtrude","SWEPT_EDGE",EDGE,{"disambiguationData":[OSD([sQuery(id+"F4.wireOp",EDGE,"E6.left"),sQuery(id+"F4.wireOp",EDGE,"E8.filletArc")])]})});
            var Q208;
            Q208=makeQuery(id+"FbWcAx6KyJmYH2d_1.4.F5.boolean.opBoolean","COPY",EDGE,{"derivedFrom":makeQuery(id+"FbWcAx6KyJmYH2d_1.4.F5.opExtrude","SWEPT_EDGE",EDGE,{"disambiguationData":[OSD([sQuery(id+"F4.wireOp",EDGE,"E6.top"),sQuery(id+"F4.wireOp",EDGE,"E10.filletArc")])]})});
            var Q209;
            Q209=makeQuery(id+"FbWcAx6KyJmYH2d_1.4.F5.boolean.opBoolean","COPY",EDGE,{"derivedFrom":makeQuery(id+"FbWcAx6KyJmYH2d_1.4.F5.opExtrude","SWEPT_EDGE",EDGE,{"disambiguationData":[OSD([sQuery(id+"F4.wireOp",EDGE,"E6.top"),sQuery(id+"F4.wireOp",EDGE,"E9.filletArc")])]})});
            var Q210;
            Q210=makeQuery(id+"FbWcAx6KyJmYH2d_1.4.F5.boolean.opBoolean","COPY",FACE,{"derivedFrom":makeQuery(id+"FbWcAx6KyJmYH2d_1.4.F5.opExtrude","SWEPT_FACE",FACE,{"disambiguationData":[OSD([sQuery(id+"F4.wireOp",EDGE,"E6.top")])]})});
            var Q211;
            Q211=makeQuery(id+"FbWcAx6KyJmYH2d_1.4.F5.boolean.opBoolean","INTERSECT",EDGE,{"derivedFrom":[makeQuery(id+"F2.opShell","OFFSET_FACE",FACE,{"disambiguationData":[OSD([sQuery(id+"F0.wireOp",EDGE,"E4")])]}),makeQuery(id+"FbWcAx6KyJmYH2d_1.4.F5.opExtrude","SWEPT_FACE",FACE,{"disambiguationData":[OSD([sQuery(id+"F4.wireOp",EDGE,"E6.right")])]})]});
            var Q212;
            Q212=makeQuery(id+"FbWcAx6KyJmYH2d_1.3.F5.boolean.opBoolean","COPY",EDGE,{"derivedFrom":makeQuery(id+"FbWcAx6KyJmYH2d_1.3.F5.opExtrude","SWEPT_EDGE",EDGE,{"disambiguationData":[OSD([sQuery(id+"F4.wireOp",EDGE,"E6.right"),sQuery(id+"F4.wireOp",EDGE,"E10.filletArc")])]})});
            var Q213;
            Q213=makeQuery(id+"FbWcAx6KyJmYH2d_1.6.F5.boolean.opBoolean","COPY",EDGE,{"derivedFrom":makeQuery(id+"FbWcAx6KyJmYH2d_1.6.F5.opExtrude","SWEPT_EDGE",EDGE,{"disambiguationData":[OSD([sQuery(id+"F4.wireOp",EDGE,"E6.right"),sQuery(id+"F4.wireOp",EDGE,"E7.filletArc")])]})});
            var Q214;
            Q214=makeQuery(id+"F5.boolean.opBoolean","INTERSECT",EDGE,{"derivedFrom":[makeQuery(id+"F1.opRevolve","SWEPT_FACE",FACE,{"disambiguationData":[OSD([sQuery(id+"F0.wireOp",EDGE,"E4")])]}),makeQuery(id+"F5.opExtrude","SWEPT_FACE",FACE,{"disambiguationData":[OSD([sQuery(id+"F4.wireOp",EDGE,"E6.left")])]})]});
            var Q215;
            Q215=makeQuery(id+"FbWcAx6KyJmYH2d_1.3.F5.boolean.opBoolean","INTERSECT",EDGE,{"derivedFrom":[makeQuery(id+"F2.opShell","OFFSET_FACE",FACE,{"disambiguationData":[OSD([sQuery(id+"F0.wireOp",EDGE,"E4")])]}),makeQuery(id+"FbWcAx6KyJmYH2d_1.3.F5.opExtrude","SWEPT_FACE",FACE,{"disambiguationData":[OSD([sQuery(id+"F4.wireOp",EDGE,"E6.top")])]})]});
            var Q216;
            Q216=makeQuery(id+"FbWcAx6KyJmYH2d_1.5.F5.boolean.opBoolean","INTERSECT",EDGE,{"derivedFrom":[makeQuery(id+"F1.opRevolve","SWEPT_FACE",FACE,{"disambiguationData":[OSD([sQuery(id+"F0.wireOp",EDGE,"E4")])]}),makeQuery(id+"FbWcAx6KyJmYH2d_1.5.F5.opExtrude","SWEPT_FACE",FACE,{"disambiguationData":[OSD([sQuery(id+"F4.wireOp",EDGE,"E9.filletArc")])]})]});
            var Q217;
            Q217=makeQuery(id+"F5.boolean.opBoolean","INTERSECT",EDGE,{"derivedFrom":[makeQuery(id+"F1.opRevolve","SWEPT_FACE",FACE,{"disambiguationData":[OSD([sQuery(id+"F0.wireOp",EDGE,"E4")])]}),makeQuery(id+"F5.opExtrude","SWEPT_FACE",FACE,{"disambiguationData":[OSD([sQuery(id+"F4.wireOp",EDGE,"E10.filletArc")])]})]});
            var Q218;
            Q218=makeQuery(id+"FbWcAx6KyJmYH2d_1.2.F5.boolean.opBoolean","COPY",FACE,{"derivedFrom":makeQuery(id+"FbWcAx6KyJmYH2d_1.2.F5.opExtrude","SWEPT_FACE",FACE,{"disambiguationData":[OSD([sQuery(id+"F4.wireOp",EDGE,"E10.filletArc")])]})});
            var Q219;
            Q219=makeQuery(id+"FbWcAx6KyJmYH2d_1.3.F5.boolean.opBoolean","COPY",EDGE,{"derivedFrom":makeQuery(id+"FbWcAx6KyJmYH2d_1.3.F5.opExtrude","SWEPT_EDGE",EDGE,{"disambiguationData":[OSD([sQuery(id+"F4.wireOp",EDGE,"E6.right"),sQuery(id+"F4.wireOp",EDGE,"E7.filletArc")])]})});
            var Q220;
            Q220=makeQuery(id+"FbWcAx6KyJmYH2d_1.2.F5.boolean.opBoolean","COPY",EDGE,{"derivedFrom":makeQuery(id+"FbWcAx6KyJmYH2d_1.2.F5.opExtrude","SWEPT_EDGE",EDGE,{"disambiguationData":[OSD([sQuery(id+"F4.wireOp",EDGE,"E6.left"),sQuery(id+"F4.wireOp",EDGE,"E8.filletArc")])]})});
            var Q221;
            Q221=makeQuery(id+"FbWcAx6KyJmYH2d_1.1.F5.boolean.opBoolean","INTERSECT",EDGE,{"derivedFrom":[makeQuery(id+"F2.opShell","OFFSET_FACE",FACE,{"disambiguationData":[OSD([sQuery(id+"F0.wireOp",EDGE,"E4")])]}),makeQuery(id+"FbWcAx6KyJmYH2d_1.1.F5.opExtrude","SWEPT_FACE",FACE,{"disambiguationData":[OSD([sQuery(id+"F4.wireOp",EDGE,"E6.left")])]})]});
            var Q222;
            Q222=makeQuery(id+"F5.boolean.opBoolean","INTERSECT",EDGE,{"derivedFrom":[makeQuery(id+"F2.opShell","OFFSET_FACE",FACE,{"disambiguationData":[OSD([sQuery(id+"F0.wireOp",EDGE,"E4")])]}),makeQuery(id+"F5.opExtrude","SWEPT_FACE",FACE,{"disambiguationData":[OSD([sQuery(id+"F4.wireOp",EDGE,"E8.filletArc")])]})]});
            var Q223;
            Q223=makeQuery(id+"FbWcAx6KyJmYH2d_1.3.F5.boolean.opBoolean","COPY",EDGE,{"derivedFrom":makeQuery(id+"FbWcAx6KyJmYH2d_1.3.F5.opExtrude","SWEPT_EDGE",EDGE,{"disambiguationData":[OSD([sQuery(id+"F4.wireOp",EDGE,"E6.left"),sQuery(id+"F4.wireOp",EDGE,"E8.filletArc")])]})});
            var Q224;
            Q224=makeQuery(id+"FbWcAx6KyJmYH2d_1.1.F5.boolean.opBoolean","INTERSECT",EDGE,{"derivedFrom":[makeQuery(id+"F2.opShell","OFFSET_FACE",FACE,{"disambiguationData":[OSD([sQuery(id+"F0.wireOp",EDGE,"E4")])]}),makeQuery(id+"FbWcAx6KyJmYH2d_1.1.F5.opExtrude","SWEPT_FACE",FACE,{"disambiguationData":[OSD([sQuery(id+"F4.wireOp",EDGE,"E7.filletArc")])]})]});
            var Q225;
            Q225=makeQuery(id+"FbWcAx6KyJmYH2d_1.2.F5.boolean.opBoolean","COPY",EDGE,{"derivedFrom":makeQuery(id+"FbWcAx6KyJmYH2d_1.2.F5.opExtrude","SWEPT_EDGE",EDGE,{"disambiguationData":[OSD([sQuery(id+"F4.wireOp",EDGE,"E6.top"),sQuery(id+"F4.wireOp",EDGE,"E9.filletArc")])]})});
            var Q226;
            Q226=makeQuery(id+"FbWcAx6KyJmYH2d_1.2.F5.boolean.opBoolean","COPY",EDGE,{"derivedFrom":makeQuery(id+"FbWcAx6KyJmYH2d_1.2.F5.opExtrude","SWEPT_EDGE",EDGE,{"disambiguationData":[OSD([sQuery(id+"F4.wireOp",EDGE,"E6.right"),sQuery(id+"F4.wireOp",EDGE,"E10.filletArc")])]})});
            var Q227;
            Q227=makeQuery(id+"FbWcAx6KyJmYH2d_1.1.F5.boolean.opBoolean","COPY",EDGE,{"derivedFrom":makeQuery(id+"FbWcAx6KyJmYH2d_1.1.F5.opExtrude","SWEPT_EDGE",EDGE,{"disambiguationData":[OSD([sQuery(id+"F4.wireOp",EDGE,"E6.right"),sQuery(id+"F4.wireOp",EDGE,"E10.filletArc")])]})});
            var Q228;
            Q228=makeQuery(id+"FbWcAx6KyJmYH2d_1.1.F5.boolean.opBoolean","COPY",EDGE,{"derivedFrom":makeQuery(id+"FbWcAx6KyJmYH2d_1.1.F5.opExtrude","SWEPT_EDGE",EDGE,{"disambiguationData":[OSD([sQuery(id+"F4.wireOp",EDGE,"E6.top"),sQuery(id+"F4.wireOp",EDGE,"E10.filletArc")])]})});
            var Q229;
            Q229=makeQuery(id+"FbWcAx6KyJmYH2d_1.1.F5.boolean.opBoolean","COPY",EDGE,{"derivedFrom":makeQuery(id+"FbWcAx6KyJmYH2d_1.1.F5.opExtrude","SWEPT_EDGE",EDGE,{"disambiguationData":[OSD([sQuery(id+"F4.wireOp",EDGE,"E6.bottom"),sQuery(id+"F4.wireOp",EDGE,"E8.filletArc")])]})});
            var Q230;
            Q230=makeQuery(id+"F5.boolean.opBoolean","INTERSECT",EDGE,{"derivedFrom":[makeQuery(id+"F2.opShell","OFFSET_FACE",FACE,{"disambiguationData":[OSD([sQuery(id+"F0.wireOp",EDGE,"E4")])]}),makeQuery(id+"F5.opExtrude","SWEPT_FACE",FACE,{"disambiguationData":[OSD([sQuery(id+"F4.wireOp",EDGE,"E6.top")])]})]});
            var Q231;
            Q231=makeQuery(id+"F5.boolean.opBoolean","COPY",EDGE,{"derivedFrom":makeQuery(id+"F5.opExtrude","SWEPT_EDGE",EDGE,{"disambiguationData":[OSD([sQuery(id+"F4.wireOp",EDGE,"E6.left"),sQuery(id+"F4.wireOp",EDGE,"E9.filletArc")])]})});
            var Q232;
            Q232=makeQuery(id+"F5.boolean.opBoolean","COPY",EDGE,{"derivedFrom":makeQuery(id+"F5.opExtrude","SWEPT_EDGE",EDGE,{"disambiguationData":[OSD([sQuery(id+"F4.wireOp",EDGE,"E6.left"),sQuery(id+"F4.wireOp",EDGE,"E8.filletArc")])]})});
            var Q233;
            Q233=makeQuery(id+"F5.boolean.opBoolean","COPY",EDGE,{"derivedFrom":makeQuery(id+"F5.opExtrude","SWEPT_EDGE",EDGE,{"disambiguationData":[OSD([sQuery(id+"F4.wireOp",EDGE,"E6.top"),sQuery(id+"F4.wireOp",EDGE,"E9.filletArc")])]})});
            var Q234;
            Q234=makeQuery(id+"F5.boolean.opBoolean","COPY",EDGE,{"derivedFrom":makeQuery(id+"F5.opExtrude","SWEPT_EDGE",EDGE,{"disambiguationData":[OSD([sQuery(id+"F4.wireOp",EDGE,"E6.top"),sQuery(id+"F4.wireOp",EDGE,"E10.filletArc")])]})});
            var Q235;
            Q235=makeQuery(id+"F5.boolean.opBoolean","COPY",EDGE,{"derivedFrom":makeQuery(id+"F5.opExtrude","SWEPT_EDGE",EDGE,{"disambiguationData":[OSD([sQuery(id+"F4.wireOp",EDGE,"E6.bottom"),sQuery(id+"F4.wireOp",EDGE,"E8.filletArc")])]})});
            var Q236;
            Q236=makeQuery(id+"F5.boolean.opBoolean","INTERSECT",EDGE,{"derivedFrom":[makeQuery(id+"F2.opShell","OFFSET_FACE",FACE,{"disambiguationData":[OSD([sQuery(id+"F0.wireOp",EDGE,"E4")])]}),makeQuery(id+"F5.opExtrude","SWEPT_FACE",FACE,{"disambiguationData":[OSD([sQuery(id+"F4.wireOp",EDGE,"E6.left")])]})]});
            var Q237;
            Q237=makeQuery(id+"FbWcAx6KyJmYH2d_1.4.F5.boolean.opBoolean","INTERSECT",EDGE,{"derivedFrom":[makeQuery(id+"F2.opShell","OFFSET_FACE",FACE,{"disambiguationData":[OSD([sQuery(id+"F0.wireOp",EDGE,"E4")])]}),makeQuery(id+"FbWcAx6KyJmYH2d_1.4.F5.opExtrude","SWEPT_FACE",FACE,{"disambiguationData":[OSD([sQuery(id+"F4.wireOp",EDGE,"E9.filletArc")])]})]});
            var Q238;
            Q238=makeQuery(id+"FbWcAx6KyJmYH2d_1.4.F5.boolean.opBoolean","INTERSECT",EDGE,{"derivedFrom":[makeQuery(id+"F2.opShell","OFFSET_FACE",FACE,{"disambiguationData":[OSD([sQuery(id+"F0.wireOp",EDGE,"E4")])]}),makeQuery(id+"FbWcAx6KyJmYH2d_1.4.F5.opExtrude","SWEPT_FACE",FACE,{"disambiguationData":[OSD([sQuery(id+"F4.wireOp",EDGE,"E7.filletArc")])]})]});
            var Q239;
            Q239=makeQuery(id+"FbWcAx6KyJmYH2d_1.1.F5.boolean.opBoolean","INTERSECT",EDGE,{"derivedFrom":[makeQuery(id+"F2.opShell","OFFSET_FACE",FACE,{"disambiguationData":[OSD([sQuery(id+"F0.wireOp",EDGE,"E4")])]}),makeQuery(id+"FbWcAx6KyJmYH2d_1.1.F5.opExtrude","SWEPT_FACE",FACE,{"disambiguationData":[OSD([sQuery(id+"F4.wireOp",EDGE,"E10.filletArc")])]})]});
            var Q240;
            Q240=makeQuery(id+"FbWcAx6KyJmYH2d_1.2.F5.boolean.opBoolean","INTERSECT",EDGE,{"derivedFrom":[makeQuery(id+"F2.opShell","OFFSET_FACE",FACE,{"disambiguationData":[OSD([sQuery(id+"F0.wireOp",EDGE,"E4")])]}),makeQuery(id+"FbWcAx6KyJmYH2d_1.2.F5.opExtrude","SWEPT_FACE",FACE,{"disambiguationData":[OSD([sQuery(id+"F4.wireOp",EDGE,"E10.filletArc")])]})]});
            var Q241;
            Q241=makeQuery(id+"F5.boolean.opBoolean","INTERSECT",EDGE,{"derivedFrom":[makeQuery(id+"F2.opShell","OFFSET_FACE",FACE,{"disambiguationData":[OSD([sQuery(id+"F0.wireOp",EDGE,"E4")])]}),makeQuery(id+"F5.opExtrude","SWEPT_FACE",FACE,{"disambiguationData":[OSD([sQuery(id+"F4.wireOp",EDGE,"E9.filletArc")])]})]});
            var Q242;
            Q242=makeQuery(id+"F5.boolean.opBoolean","INTERSECT",EDGE,{"derivedFrom":[makeQuery(id+"F1.opRevolve","SWEPT_FACE",FACE,{"disambiguationData":[OSD([sQuery(id+"F0.wireOp",EDGE,"E4")])]}),makeQuery(id+"F5.opExtrude","SWEPT_FACE",FACE,{"disambiguationData":[OSD([sQuery(id+"F4.wireOp",EDGE,"E8.filletArc")])]})]});
            var Q243;
            Q243=makeQuery(id+"FbWcAx6KyJmYH2d_1.6.F5.boolean.opBoolean","INTERSECT",EDGE,{"derivedFrom":[makeQuery(id+"F2.opShell","OFFSET_FACE",FACE,{"disambiguationData":[OSD([sQuery(id+"F0.wireOp",EDGE,"E4")])]}),makeQuery(id+"FbWcAx6KyJmYH2d_1.6.F5.opExtrude","SWEPT_FACE",FACE,{"disambiguationData":[OSD([sQuery(id+"F4.wireOp",EDGE,"E6.top")])]})]});
            var Q244;
            Q244=makeQuery(id+"FbWcAx6KyJmYH2d_1.6.F5.boolean.opBoolean","COPY",EDGE,{"derivedFrom":makeQuery(id+"FbWcAx6KyJmYH2d_1.6.F5.opExtrude","SWEPT_EDGE",EDGE,{"disambiguationData":[OSD([sQuery(id+"F4.wireOp",EDGE,"E6.right"),sQuery(id+"F4.wireOp",EDGE,"E10.filletArc")])]})});
            var Q245;
            Q245=makeQuery(id+"FbWcAx6KyJmYH2d_1.6.F5.boolean.opBoolean","COPY",EDGE,{"derivedFrom":makeQuery(id+"FbWcAx6KyJmYH2d_1.6.F5.opExtrude","SWEPT_EDGE",EDGE,{"disambiguationData":[OSD([sQuery(id+"F4.wireOp",EDGE,"E6.top"),sQuery(id+"F4.wireOp",EDGE,"E10.filletArc")])]})});
            var Q246;
            Q246=makeQuery(id+"FbWcAx6KyJmYH2d_1.6.F5.boolean.opBoolean","COPY",EDGE,{"derivedFrom":makeQuery(id+"FbWcAx6KyJmYH2d_1.6.F5.opExtrude","SWEPT_EDGE",EDGE,{"disambiguationData":[OSD([sQuery(id+"F4.wireOp",EDGE,"E6.top"),sQuery(id+"F4.wireOp",EDGE,"E9.filletArc")])]})});
            var Q247;
            Q247=makeQuery(id+"FbWcAx6KyJmYH2d_1.5.F5.boolean.opBoolean","COPY",EDGE,{"derivedFrom":makeQuery(id+"FbWcAx6KyJmYH2d_1.5.F5.opExtrude","SWEPT_EDGE",EDGE,{"disambiguationData":[OSD([sQuery(id+"F4.wireOp",EDGE,"E6.left"),sQuery(id+"F4.wireOp",EDGE,"E9.filletArc")])]})});
            var Q248;
            Q248=makeQuery(id+"FbWcAx6KyJmYH2d_1.5.F5.boolean.opBoolean","COPY",EDGE,{"derivedFrom":makeQuery(id+"FbWcAx6KyJmYH2d_1.5.F5.opExtrude","SWEPT_EDGE",EDGE,{"disambiguationData":[OSD([sQuery(id+"F4.wireOp",EDGE,"E6.top"),sQuery(id+"F4.wireOp",EDGE,"E10.filletArc")])]})});
            var Q249;
            Q249=makeQuery(id+"FbWcAx6KyJmYH2d_1.5.F5.boolean.opBoolean","COPY",EDGE,{"derivedFrom":makeQuery(id+"FbWcAx6KyJmYH2d_1.5.F5.opExtrude","SWEPT_EDGE",EDGE,{"disambiguationData":[OSD([sQuery(id+"F4.wireOp",EDGE,"E6.top"),sQuery(id+"F4.wireOp",EDGE,"E9.filletArc")])]})});
            var Q250;
            Q250=makeQuery(id+"FbWcAx6KyJmYH2d_1.5.F5.boolean.opBoolean","COPY",EDGE,{"derivedFrom":makeQuery(id+"FbWcAx6KyJmYH2d_1.5.F5.opExtrude","SWEPT_EDGE",EDGE,{"disambiguationData":[OSD([sQuery(id+"F4.wireOp",EDGE,"E6.bottom"),sQuery(id+"F4.wireOp",EDGE,"E7.filletArc")])]})});
            var Q251;
            Q251=makeQuery(id+"FbWcAx6KyJmYH2d_1.4.F5.boolean.opBoolean","COPY",EDGE,{"derivedFrom":makeQuery(id+"FbWcAx6KyJmYH2d_1.4.F5.opExtrude","SWEPT_EDGE",EDGE,{"disambiguationData":[OSD([sQuery(id+"F4.wireOp",EDGE,"E6.right"),sQuery(id+"F4.wireOp",EDGE,"E7.filletArc")])]})});
            var Q252;
            Q252=makeQuery(id+"FbWcAx6KyJmYH2d_1.4.F5.boolean.opBoolean","COPY",EDGE,{"derivedFrom":makeQuery(id+"FbWcAx6KyJmYH2d_1.4.F5.opExtrude","SWEPT_EDGE",EDGE,{"disambiguationData":[OSD([sQuery(id+"F4.wireOp",EDGE,"E6.left"),sQuery(id+"F4.wireOp",EDGE,"E9.filletArc")])]})});
            var Q253;
            Q253=makeQuery(id+"FbWcAx6KyJmYH2d_1.5.F5.boolean.opBoolean","INTERSECT",EDGE,{"derivedFrom":[makeQuery(id+"F1.opRevolve","SWEPT_FACE",FACE,{"disambiguationData":[OSD([sQuery(id+"F0.wireOp",EDGE,"E4")])]}),makeQuery(id+"FbWcAx6KyJmYH2d_1.5.F5.opExtrude","SWEPT_FACE",FACE,{"disambiguationData":[OSD([sQuery(id+"F4.wireOp",EDGE,"E7.filletArc")])]})]});
            var Q254;
            Q254=makeQuery(id+"FbWcAx6KyJmYH2d_1.5.F5.boolean.opBoolean","INTERSECT",EDGE,{"derivedFrom":[makeQuery(id+"F2.opShell","OFFSET_FACE",FACE,{"disambiguationData":[OSD([sQuery(id+"F0.wireOp",EDGE,"E4")])]}),makeQuery(id+"FbWcAx6KyJmYH2d_1.5.F5.opExtrude","SWEPT_FACE",FACE,{"disambiguationData":[OSD([sQuery(id+"F4.wireOp",EDGE,"E6.top")])]})]});
            var Q255;
            Q255=makeQuery(id+"FbWcAx6KyJmYH2d_1.5.F5.boolean.opBoolean","INTERSECT",EDGE,{"derivedFrom":[makeQuery(id+"F2.opShell","OFFSET_FACE",FACE,{"disambiguationData":[OSD([sQuery(id+"F0.wireOp",EDGE,"E4")])]}),makeQuery(id+"FbWcAx6KyJmYH2d_1.5.F5.opExtrude","SWEPT_FACE",FACE,{"disambiguationData":[OSD([sQuery(id+"F4.wireOp",EDGE,"E10.filletArc")])]})]});
            fillet(context, id + "F6", {"entities" : qUnion([Q0, Q1, Q2, Q3, Q4, Q5, Q6, Q7, Q8, Q9, Q10, Q11, Q12, Q13, Q14, Q15, Q16, Q17, Q18, Q19, Q20, Q21, Q22, Q23, Q24, Q25, Q26, Q27, Q28, Q29, Q30, Q31, Q32, Q33, Q34, Q35, Q36, Q37, Q38, Q39, Q40, Q41, Q42, Q43, Q44, Q45, Q46, Q47, Q48, Q49, Q50, Q51, Q52, Q53, Q54, Q55, Q56, Q57, Q58, Q59, Q60, Q61, Q62, Q63, Q64, Q65, Q66, Q67, Q68, Q69, Q70, Q71, Q72, Q73, Q74, Q75, Q76, Q77, Q78, Q79, Q80, Q81, Q82, Q83, Q84, Q85, Q86, Q87, Q88, Q89, Q90, Q91, Q92, Q93, Q94, Q95, Q96, Q97, Q98, Q99, Q100, Q101, Q102, Q103, Q104, Q105, Q106, Q107, Q108, Q109, Q110, Q111, Q112, Q113, Q114, Q115, Q116, Q117, Q118, Q119, Q120, Q121, Q122, Q123, Q124, Q125, Q126, Q127, Q128, Q129, Q130, Q131, Q132, Q133, Q134, Q135, Q136, Q137, Q138, Q139, Q140, Q141, Q142, Q143, Q144, Q145, Q146, Q147, Q148, Q149, Q150, Q151, Q152, Q153, Q154, Q155, Q156, Q157, Q158, Q159, Q160, Q161, Q162, Q163, Q164, Q165, Q166, Q167, Q168, Q169, Q170, Q171, Q172, Q173, Q174, Q175, Q176, Q177, Q178, Q179, Q180, Q181, Q182, Q183, Q184, Q185, Q186, Q187, Q188, Q189, Q190, Q191, Q192, Q193, Q194, Q195, Q196, Q197, Q198, Q199, Q200, Q201, Q202, Q203, Q204, Q205, Q206, Q207, Q208, Q209, Q210, Q211, Q212, Q213, Q214, Q215, Q216, Q217, Q218, Q219, Q220, Q221, Q222, Q223, Q224, Q225, Q226, Q227, Q228, Q229, Q230, Q231, Q232, Q233, Q234, Q235, Q236, Q237, Q238, Q239, Q240, Q241, Q242, Q243, Q244, Q245, Q246, Q247, Q248, Q249, Q250, Q251, Q252, Q253, Q254, Q255]), "radius" : 0.15 * mm, "tangentPropagation" : true, "allowEdgeOverflow" : false});
        }
    });
